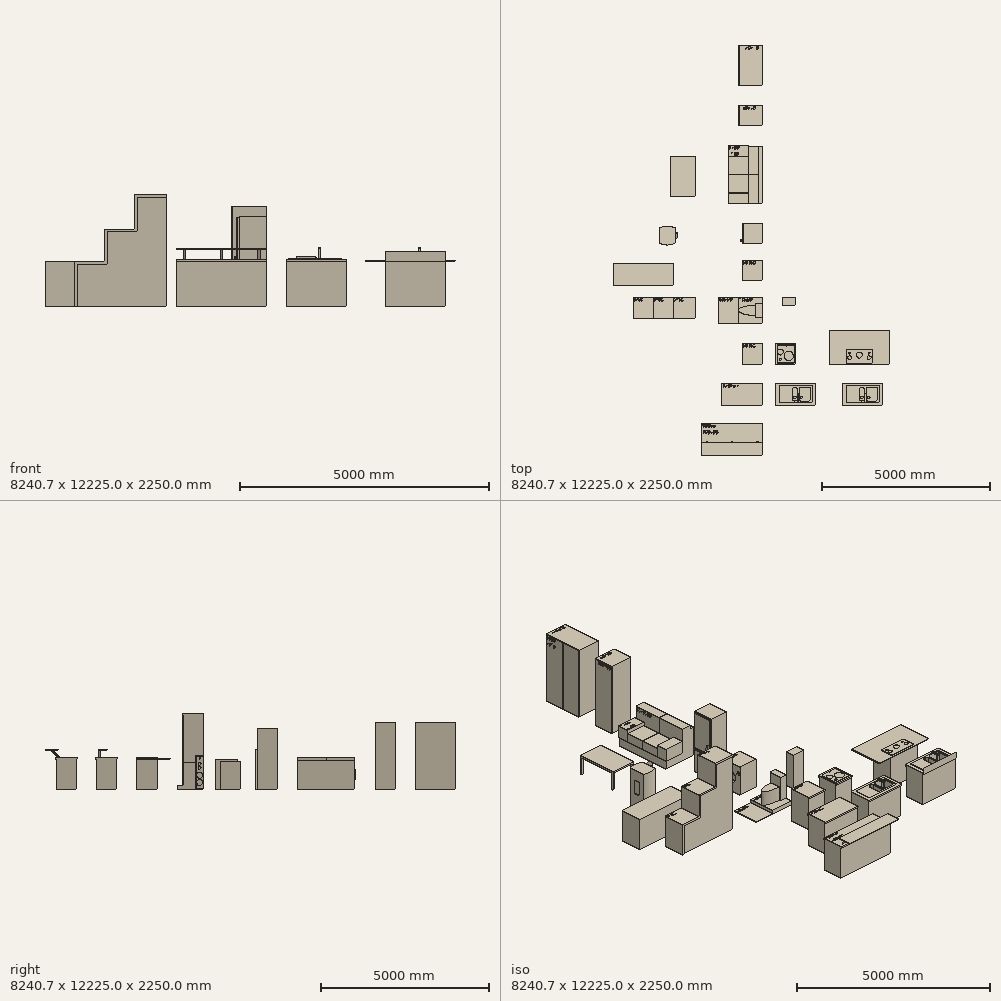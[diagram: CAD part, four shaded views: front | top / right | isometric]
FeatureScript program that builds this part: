
annotation { "Feature Type Name" : "Feature", "Feature Type Description" : "" }
export const myFeature = defineFeature(function(context is Context, id is Id, definition is map)
    precondition{}
    {
        {
            var Q0;
            Q0=qCreatedBy(makeId("Top.planeOp"),FACE);
            var sketch = newSketch(context, id + "F0", { "sketchPlane" : qUnion([Q0])});
            skLineSegment(sketch, "E0.bottom", {"start": v(0, 0) * mm, "end": v(-1300, 0) * mm});
            skLineSegment(sketch, "E0.top", {"start": v(0, -800) * mm, "end": v(-1300, -800) * mm});
            skLineSegment(sketch, "E0.left", {"start": v(0, 0) * mm, "end": v(0, -800) * mm});
            skLineSegment(sketch, "E0.right", {"start": v(-1300, 0) * mm, "end": v(-1300, -800) * mm});
            skSolve(sketch);
        }
        {
            var Q0;
            Q0 = qSketchRegion(id + "F0", true);
            extrude(context, id + "F1", {"entities" : qUnion([Q0]), "depth" : 11 * mm});
        }
        {
            var Q0;
            Q0=makeQuery(id+"F1.opExtrude","CAP_FACE",FACE,{"disambiguationData":[OSD([sQuery(id+"F0.wireOp",EDGE,"E0.bottom"),sQuery(id+"F0.wireOp",EDGE,"E0.top"),sQuery(id+"F0.wireOp",EDGE,"E0.left"),sQuery(id+"F0.wireOp",EDGE,"E0.right")])],"isStart":false});
            var sketch = newSketch(context, id + "F2", { "sketchPlane" : qUnion([Q0])});
            skLineSegment(sketch, "E1.bottom", {"start": v(0, 0) * mm, "end": v(-700, 0) * mm});
            skLineSegment(sketch, "E1.top", {"start": v(0, -800) * mm, "end": v(-700, -800) * mm});
            skLineSegment(sketch, "E1.left", {"start": v(0, 0) * mm, "end": v(0, -800) * mm});
            skLineSegment(sketch, "E1.right", {"start": v(-700, 0) * mm, "end": v(-700, -800) * mm});
            skSolve(sketch);
        }
        {
            var Q0;
            Q0 = qSketchRegion(id + "F2", true);
            extrude(context, id + "F3", {"entities" : qUnion([Q0]), "operationType" : NewBodyOperationType.ADD, "depth" : 100 * mm});
        }
        {
            var Q0;
            Q0=makeQuery(id+"F3.opExtrude","CAP_FACE",FACE,{"disambiguationData":[OSD([sQuery(id+"F2.wireOp",EDGE,"E1.bottom"),sQuery(id+"F2.wireOp",EDGE,"E1.top"),sQuery(id+"F2.wireOp",EDGE,"E1.left"),sQuery(id+"F2.wireOp",EDGE,"E1.right")])],"isStart":false});
            var sketch = newSketch(context, id + "F4", { "sketchPlane" : qUnion([Q0])});
            skLineSegment(sketch, "E2.bottom", {"start": v(0, -200) * mm, "end": v(-200, -200) * mm});
            skLineSegment(sketch, "E2.top", {"start": v(0, -600) * mm, "end": v(-200, -600) * mm});
            skLineSegment(sketch, "E2.left", {"start": v(0, -200) * mm, "end": v(0, -600) * mm});
            skLineSegment(sketch, "E2.right", {"start": v(-200, -200) * mm, "end": v(-200, -600) * mm});
            skSolve(sketch);
        }
        {
            var Q0;
            {var subQ2=sQuery(id+"F4.wireOp",EDGE,"E2.bottom");Q0=makeQuery(id+"F4.imprint","IMPRINT",FACE,{"disambiguationData":[TD([[makeQuery(id+"F4.imprint","IMPRINT",EDGE,{"derivedFrom":subQ2}),-1.0]])]});}
            var sketch = newSketch(context, id + "F5", { "sketchPlane" : qUnion([Q0])});
            skLineSegment(sketch, "E3", {"start": v(-200, -249.1) * mm, "end": v(-200, -549.1) * mm});
            skEllipticalArc(sketch, "E4", {});
            const initialGuessF5  = {"E4": [-0.2, -0.3990970113503016, 1, 0, 0.5000090601184898, 0.15, 1.5707963267948966, 4.71238898038469]};
            skSetInitialGuess(sketch, initialGuessF5);
            skSolve(sketch);
        }
        {
            var Q0;
            Q0 = qSketchRegion(id + "F4", true);
            extrude(context, id + "F6", {"entities" : qUnion([Q0]), "operationType" : NewBodyOperationType.ADD, "depth" : 700 * mm});
        }
        {
            var Q0;
            {var subQ0=sQuery(id+"F5.wireOp",EDGE,"E3");Q0=makeQuery(id+"F5.imprint","IMPRINT",FACE,{"disambiguationData":[TD([[makeQuery(id+"F5.imprint","IMPRINT",EDGE,{"derivedFrom":subQ0}),-1.0]])]});}
            extrude(context, id + "F7", {"entities" : qUnion([Q0]), "operationType" : NewBodyOperationType.ADD, "depth" : 400 * mm});
        }
        {
            var Q0;
            Q0=makeQuery(id+"F1.opExtrude","CAP_FACE",FACE,{"disambiguationData":[OSD([sQuery(id+"F0.wireOp",EDGE,"E0.bottom"),sQuery(id+"F0.wireOp",EDGE,"E0.top"),sQuery(id+"F0.wireOp",EDGE,"E0.left"),sQuery(id+"F0.wireOp",EDGE,"E0.right")])],"isStart":false});
            var sketch = newSketch(context, id + "F8", { "sketchPlane" : qUnion([Q0])});
            skText(sketch, "E5", { "text": "60x80", "fontName": "OpenSans-Regular.ttf"});
            const initialGuessF8  = {"E5": [-1.28, -0.12, 1, 0, 0.1]};
            skSetInitialGuess(sketch, initialGuessF8);
            skSolve(sketch);
        }
        {
            var Q0;
            Q0 = qSketchRegion(id + "F8", true);
            extrude(context, id + "F9", {"entities" : qUnion([Q0]), "operationType" : NewBodyOperationType.REMOVE, "oppositeDirection" : true, "depth" : 10 * mm});
        }
        {
            var Q0;
            {var subQ0=sQuery(id+"F2.wireOp",EDGE,"E1.left");var subQ1=sQuery(id+"F2.wireOp",EDGE,"E1.bottom");var subQ3=sQuery(id+"F2.wireOp",EDGE,"E1.right");Q0=makeQuery(id+"F7.boolean.opBoolean","SPLIT",FACE,{"disambiguationData":[TD([makeQuery(id+"F1.opExtrude","SWEPT_FACE",FACE,{"disambiguationData":[OSD([sQuery(id+"F0.wireOp",EDGE,"E0.bottom")])]})])],"derivedFrom":makeQuery(id+"F3.opExtrude","CAP_FACE",FACE,{"disambiguationData":[OSD([subQ1,sQuery(id+"F2.wireOp",EDGE,"E1.top"),subQ0,subQ3])],"isStart":false})});}
            var sketch = newSketch(context, id + "F10", { "sketchPlane" : qUnion([Q0])});
            skText(sketch, "E6", { "text": "70x80", "fontName": "OpenSans-Regular.ttf"});
            const initialGuessF10  = {"E6": [-0.68, -0.12, 1, 0, 0.1]};
            skSetInitialGuess(sketch, initialGuessF10);
            skSolve(sketch);
        }
        {
            var Q0;
            Q0 = qSketchRegion(id + "F10", true);
            extrude(context, id + "F11", {"entities" : qUnion([Q0]), "operationType" : NewBodyOperationType.REMOVE, "oppositeDirection" : true, "depth" : 10 * mm});
        }
        {
            var Q0;
            Q0=qCreatedBy(makeId("Top.planeOp"),FACE);
            var sketch = newSketch(context, id + "F12", { "sketchPlane" : qUnion([Q0])});
            skLineSegment(sketch, "E7.bottom", {"start": v(0, 500) * mm, "end": v(-600, 500) * mm});
            skLineSegment(sketch, "E7.top", {"start": v(0, 1100) * mm, "end": v(-600, 1100) * mm});
            skLineSegment(sketch, "E7.left", {"start": v(0, 500) * mm, "end": v(0, 1100) * mm});
            skLineSegment(sketch, "E7.right", {"start": v(-600, 500) * mm, "end": v(-600, 1100) * mm});
            skSolve(sketch);
        }
        {
            var Q0;
            Q0 = qSketchRegion(id + "F12", true);
            extrude(context, id + "F13", {"entities" : qUnion([Q0]), "depth" : 830 * mm});
        }
        {
            var Q0;
            Q0=makeQuery(id+"F13.opExtrude","SWEPT_FACE",FACE,{"disambiguationData":[OSD([sQuery(id+"F12.wireOp",EDGE,"E7.right")])]});
            var sketch = newSketch(context, id + "F14", { "sketchPlane" : qUnion([Q0])});
            skCircle(sketch, "E8", {"center": v(-800, 415) * mm, "radius": 150 * mm});
            skLineSegment(sketch, "E9", {"start": v(-1100, 415) * mm, "end": v(-500, 415) * mm, "construction": true});
            skLineSegment(sketch, "E10", {"start": v(-800, 0) * mm, "end": v(-800, 830) * mm, "construction": true});
            skSolve(sketch);
        }
        {
            var Q0;
            Q0=makeQuery(id+"F14.imprint","IMPRINT",FACE,{"disambiguationData":[TD([[makeQuery(id+"F14.imprint","IMPRINT",EDGE,{"derivedFrom":sQuery(id+"F14.wireOp",EDGE,"E8")}),1.0]])]});
            extrude(context, id + "F15", {"entities" : qUnion([Q0]), "operationType" : NewBodyOperationType.REMOVE, "oppositeDirection" : true, "depth" : 100 * mm});
        }
        {
            var Q0;
            Q0=makeQuery(id+"F13.opExtrude","CAP_FACE",FACE,{"disambiguationData":[OSD([sQuery(id+"F12.wireOp",EDGE,"E7.bottom"),sQuery(id+"F12.wireOp",EDGE,"E7.top"),sQuery(id+"F12.wireOp",EDGE,"E7.left"),sQuery(id+"F12.wireOp",EDGE,"E7.right")])],"isStart":false});
            var sketch = newSketch(context, id + "F16", { "sketchPlane" : qUnion([Q0])});
            skText(sketch, "E11", { "text": "60x60\n", "fontName": "OpenSans-Regular.ttf"});
            const initialGuessF16  = {"E11": [-0.58, 0.98, 1, 0, 0.1]};
            skSetInitialGuess(sketch, initialGuessF16);
            skSolve(sketch);
        }
        {
            var Q0;
            Q0 = qSketchRegion(id + "F16", true);
            extrude(context, id + "F17", {"entities" : qUnion([Q0]), "operationType" : NewBodyOperationType.REMOVE, "oppositeDirection" : true, "depth" : 10 * mm});
        }
        {
            var Q0;
            Q0=qCreatedBy(makeId("Front.planeOp"),FACE);
            var sketch = newSketch(context, id + "F18", { "sketchPlane" : qUnion([Q0])});
            skLineSegment(sketch, "E12", {"start": v(-2000, 2250) * mm, "end": v(-2000, 2200) * mm});
            skLineSegment(sketch, "E13", {"start": v(-2000, 2200) * mm, "end": v(-2600, 2200) * mm});
            skLineSegment(sketch, "E14", {"start": v(-2600, 2200) * mm, "end": v(-2600, 1500) * mm});
            skLineSegment(sketch, "E15", {"start": v(-2600, 1500) * mm, "end": v(-3200, 1500) * mm});
            skLineSegment(sketch, "E16", {"start": v(-3200, 1500) * mm, "end": v(-3200, 850) * mm});
            skLineSegment(sketch, "E17", {"start": v(-3200, 850) * mm, "end": v(-3800, 850) * mm});
            skLineSegment(sketch, "E18", {"start": v(-3800, 850) * mm, "end": v(-3800, 0) * mm});
            skLineSegment(sketch, "E19", {"start": v(-3800, 0) * mm, "end": v(-3850, 0) * mm});
            skLineSegment(sketch, "E20", {"start": v(-3850, 0) * mm, "end": v(-3850, 900) * mm});
            skLineSegment(sketch, "E21", {"start": v(-3850, 900) * mm, "end": v(-3250, 900) * mm});
            skLineSegment(sketch, "E22", {"start": v(-3250, 900) * mm, "end": v(-3250, 1550) * mm});
            skLineSegment(sketch, "E23", {"start": v(-3250, 1550) * mm, "end": v(-2650, 1550) * mm});
            skLineSegment(sketch, "E24", {"start": v(-2650, 1550) * mm, "end": v(-2650, 2250) * mm});
            skLineSegment(sketch, "E25", {"start": v(-2650, 2250) * mm, "end": v(-2000, 2250) * mm});
            skSolve(sketch);
        }
        {
            var Q0;
            Q0 = qSketchRegion(id + "F18", true);
            extrude(context, id + "F19", {"entities" : qUnion([Q0]), "depth" : 650 * mm});
        }
        {
            var Q0;
            Q0=makeQuery(id+"F19.opExtrude","SWEPT_FACE",FACE,{"disambiguationData":[OSD([sQuery(id+"F18.wireOp",EDGE,"E13")])]});
            var sketch = newSketch(context, id + "F20", { "sketchPlane" : qUnion([Q0])});
            skLineSegment(sketch, "E26.bottom", {"start": v(-2000, 625) * mm, "end": v(-2600, 625) * mm});
            skLineSegment(sketch, "E26.top", {"start": v(-2000, 25) * mm, "end": v(-2600, 25) * mm});
            skLineSegment(sketch, "E26.left", {"start": v(-2000, 625) * mm, "end": v(-2000, 25) * mm});
            skLineSegment(sketch, "E26.right", {"start": v(-2600, 625) * mm, "end": v(-2600, 25) * mm});
            skSolve(sketch);
        }
        {
            var Q0;
            Q0 = qSketchRegion(id + "F20", true);
            var Q1;
            Q1=qCreatedBy(makeId("Top.planeOp"),FACE);
            extrude(context, id + "F21", {"entities" : qUnion([Q0]), "operationType" : NewBodyOperationType.ADD, "endBound" : BoundingType.UP_TO_SURFACE, "endBoundEntityFace" : qUnion([Q1]), "depth" : 25 * mm});
        }
        {
            var Q0;
            Q0=makeQuery(id+"F19.opExtrude","SWEPT_FACE",FACE,{"disambiguationData":[OSD([sQuery(id+"F18.wireOp",EDGE,"E15")])]});
            var sketch = newSketch(context, id + "F22", { "sketchPlane" : qUnion([Q0])});
            skLineSegment(sketch, "E27.bottom", {"start": v(-2600, 25) * mm, "end": v(-3200, 25) * mm});
            skLineSegment(sketch, "E27.top", {"start": v(-2600, 625) * mm, "end": v(-3200, 625) * mm});
            skLineSegment(sketch, "E27.left", {"start": v(-2600, 25) * mm, "end": v(-2600, 625) * mm});
            skLineSegment(sketch, "E27.right", {"start": v(-3200, 25) * mm, "end": v(-3200, 625) * mm});
            skSolve(sketch);
        }
        {
            var Q0;
            Q0=makeQuery(id+"F22.imprint","IMPRINT",FACE,{"disambiguationData":[TD([[makeQuery(id+"F22.imprint","IMPRINT",EDGE,{"derivedFrom":sQuery(id+"F22.wireOp",EDGE,"E27.bottom")}),-1.0]])]});
            var Q1;
            Q1=qCreatedBy(makeId("Top.planeOp"),FACE);
            extrude(context, id + "F23", {"entities" : qUnion([Q0]), "operationType" : NewBodyOperationType.ADD, "endBound" : BoundingType.UP_TO_SURFACE, "endBoundEntityFace" : qUnion([Q1]), "depth" : 25 * mm});
        }
        {
            var Q0;
            Q0=makeQuery(id+"F19.opExtrude","SWEPT_FACE",FACE,{"disambiguationData":[OSD([sQuery(id+"F18.wireOp",EDGE,"E17")])]});
            var sketch = newSketch(context, id + "F24", { "sketchPlane" : qUnion([Q0])});
            skLineSegment(sketch, "E28.bottom", {"start": v(-3200, 25) * mm, "end": v(-3800, 25) * mm});
            skLineSegment(sketch, "E28.top", {"start": v(-3200, 625) * mm, "end": v(-3800, 625) * mm});
            skLineSegment(sketch, "E28.left", {"start": v(-3200, 25) * mm, "end": v(-3200, 625) * mm});
            skLineSegment(sketch, "E28.right", {"start": v(-3800, 25) * mm, "end": v(-3800, 625) * mm});
            skSolve(sketch);
        }
        {
            var Q0;
            Q0=makeQuery(id+"F24.imprint","IMPRINT",FACE,{"disambiguationData":[TD([[makeQuery(id+"F24.imprint","IMPRINT",EDGE,{"derivedFrom":sQuery(id+"F24.wireOp",EDGE,"E28.bottom")}),-1.0]])]});
            var Q1;
            Q1=qCreatedBy(makeId("Top.planeOp"),FACE);
            extrude(context, id + "F25", {"entities" : qUnion([Q0]), "operationType" : NewBodyOperationType.ADD, "endBound" : BoundingType.UP_TO_SURFACE, "endBoundEntityFace" : qUnion([Q1]), "depth" : 25 * mm});
        }
        {
            var Q0;
            Q0=makeQuery(id+"F19.opExtrude","CAP_FACE",FACE,{"disambiguationData":[OSD([sQuery(id+"F18.wireOp",EDGE,"E12"),sQuery(id+"F18.wireOp",EDGE,"E13"),sQuery(id+"F18.wireOp",EDGE,"E14"),sQuery(id+"F18.wireOp",EDGE,"E15"),sQuery(id+"F18.wireOp",EDGE,"E16"),sQuery(id+"F18.wireOp",EDGE,"E17"),sQuery(id+"F18.wireOp",EDGE,"E18"),sQuery(id+"F18.wireOp",EDGE,"E19"),sQuery(id+"F18.wireOp",EDGE,"E20"),sQuery(id+"F18.wireOp",EDGE,"E21"),sQuery(id+"F18.wireOp",EDGE,"E22"),sQuery(id+"F18.wireOp",EDGE,"E23"),sQuery(id+"F18.wireOp",EDGE,"E24"),sQuery(id+"F18.wireOp",EDGE,"E25")])],"isStart":true});
            var sketch = newSketch(context, id + "F26", { "sketchPlane" : qUnion([Q0])});
            skLineSegment(sketch, "E29.bottom", {"start": v(3850, 0) * mm, "end": v(2000, 0) * mm});
            skLineSegment(sketch, "E29.top", {"start": v(3850, 50) * mm, "end": v(3800, 50) * mm});
            skLineSegment(sketch, "E29.left", {"start": v(3850, 0) * mm, "end": v(3850, 50) * mm});
            skLineSegment(sketch, "E29.right", {"start": v(2000, 0) * mm, "end": v(2000, 50) * mm});
            skLineSegment(sketch, "E30.bottom", {"start": v(2600, 2200) * mm, "end": v(2599, 2200) * mm});
            skLineSegment(sketch, "E30.left", {"start": v(2600, 2200) * mm, "end": v(2600, 50) * mm});
            skLineSegment(sketch, "E30.right", {"start": v(2599, 2200) * mm, "end": v(2599, 50) * mm});
            skLineSegment(sketch, "E31.bottom", {"start": v(3200, 1500) * mm, "end": v(3199, 1500) * mm});
            skLineSegment(sketch, "E31.left", {"start": v(3200, 1500) * mm, "end": v(3200, 50) * mm});
            skLineSegment(sketch, "E31.right", {"start": v(3199, 1500) * mm, "end": v(3199, 50) * mm});
            skLineSegment(sketch, "E32.bottom", {"start": v(3800, 850) * mm, "end": v(3799, 850) * mm});
            skLineSegment(sketch, "E32.left", {"start": v(3800, 850) * mm, "end": v(3800, 50) * mm});
            skLineSegment(sketch, "E32.right", {"start": v(3799, 850) * mm, "end": v(3799, 50) * mm});
            skLineSegment(sketch, "E33.trimOffspring", {"start": v(2599, 50) * mm, "end": v(2000, 50) * mm});
            skLineSegment(sketch, "E34.trimOffspring", {"start": v(3199, 50) * mm, "end": v(2600, 50) * mm});
            skLineSegment(sketch, "E35.trimOffspring", {"start": v(3799, 50) * mm, "end": v(3200, 50) * mm});
            skSolve(sketch);
        }
        {
            var Q0;
            {var subQ10=sQuery(id+"F26.wireOp",EDGE,"E29.right");Q0=makeQuery(id+"F26.imprint","IMPRINT",FACE,{"disambiguationData":[TD([[makeQuery(id+"F26.imprint","IMPRINT",EDGE,{"derivedFrom":subQ10}),-1.0]])]});}
            extrude(context, id + "F27", {"entities" : qUnion([Q0]), "operationType" : NewBodyOperationType.REMOVE, "oppositeDirection" : true, "depth" : 35 * mm});
        }
        {
            var Q0;
            Q0=makeQuery(id+"F19.opExtrude","SWEPT_FACE",FACE,{"disambiguationData":[OSD([sQuery(id+"F18.wireOp",EDGE,"E25")])]});
            var sketch = newSketch(context, id + "F28", { "sketchPlane" : qUnion([Q0])});
            skText(sketch, "E36", { "text": "65x65", "fontName": "OpenSans-Regular.ttf"});
            const initialGuessF28  = {"E36": [-2.71922, -0.12, 1, 0, 0.1]};
            skSetInitialGuess(sketch, initialGuessF28);
            skSolve(sketch);
        }
        {
            var Q0;
            Q0 = qSketchRegion(id + "F28", true);
            extrude(context, id + "F29", {"entities" : qUnion([Q0]), "operationType" : NewBodyOperationType.REMOVE, "oppositeDirection" : true, "depth" : 10 * mm});
        }
        {
            var Q0;
            Q0=makeQuery(id+"F19.opExtrude","SWEPT_FACE",FACE,{"disambiguationData":[OSD([sQuery(id+"F18.wireOp",EDGE,"E23")])]});
            var sketch = newSketch(context, id + "F30", { "sketchPlane" : qUnion([Q0])});
            skText(sketch, "E37", { "text": "60x65", "fontName": "OpenSans-Regular.ttf"});
            const initialGuessF30  = {"E37": [-3.31922, -0.12, 1, 0, 0.1]};
            skSetInitialGuess(sketch, initialGuessF30);
            skSolve(sketch);
        }
        {
            var Q0;
            Q0 = qSketchRegion(id + "F30", true);
            extrude(context, id + "F31", {"entities" : qUnion([Q0]), "operationType" : NewBodyOperationType.REMOVE, "oppositeDirection" : true, "depth" : 10 * mm});
        }
        {
            var Q0;
            Q0=makeQuery(id+"F19.opExtrude","SWEPT_FACE",FACE,{"disambiguationData":[OSD([sQuery(id+"F18.wireOp",EDGE,"E21")])]});
            var sketch = newSketch(context, id + "F32", { "sketchPlane" : qUnion([Q0])});
            skText(sketch, "E38", { "text": "60x65", "fontName": "OpenSans-Regular.ttf"});
            const initialGuessF32  = {"E38": [-3.91922, -0.12, 1, 0, 0.1]};
            skSetInitialGuess(sketch, initialGuessF32);
            skSolve(sketch);
        }
        {
            var Q0;
            Q0 = qSketchRegion(id + "F32", true);
            extrude(context, id + "F33", {"entities" : qUnion([Q0]), "operationType" : NewBodyOperationType.REMOVE, "oppositeDirection" : true, "depth" : 10 * mm});
        }
        {
            var Q0;
            Q0=makeQuery(id+"F27.boolean.opBoolean","SPLIT",FACE,{"disambiguationData":[TD([makeQuery(id+"F19.opExtrude","SWEPT_FACE",FACE,{"disambiguationData":[OSD([sQuery(id+"F18.wireOp",EDGE,"E12")])]})])],"derivedFrom":makeQuery(id+"F25.boolean.opBoolean","MERGE",FACE,{"derivedFrom":[makeQuery(id+"F23.boolean.opBoolean","MERGE",FACE,{"derivedFrom":[makeQuery(id+"F21.opExtrude","SWEPT_FACE",FACE,{"disambiguationData":[OSD([sQuery(id+"F20.wireOp",EDGE,"E26.top")])]}),makeQuery(id+"F23.opExtrude","SWEPT_FACE",FACE,{"disambiguationData":[OSD([sQuery(id+"F22.wireOp",EDGE,"E27.bottom")])]})]}),makeQuery(id+"F25.opExtrude","SWEPT_FACE",FACE,{"disambiguationData":[OSD([sQuery(id+"F24.wireOp",EDGE,"E28.bottom")])]})]})});
            var sketch = newSketch(context, id + "F34", { "sketchPlane" : qUnion([Q0])});
            skText(sketch, "E39", { "text": "2200x60", "fontName": "OpenSans-Regular.ttf"});
            const initialGuessF34  = {"E39": [2.10922, 2.08, 1, 0, 0.1]};
            skSetInitialGuess(sketch, initialGuessF34);
            skSolve(sketch);
        }
        {
            var Q0;
            Q0 = qSketchRegion(id + "F34", true);
            extrude(context, id + "F35", {"entities" : qUnion([Q0]), "operationType" : NewBodyOperationType.REMOVE, "oppositeDirection" : true, "depth" : 10 * mm});
        }
        {
            var Q0;
            Q0=makeQuery(id+"F27.boolean.opBoolean","SPLIT",FACE,{"disambiguationData":[TD([makeQuery(id+"F19.opExtrude","SWEPT_FACE",FACE,{"disambiguationData":[OSD([sQuery(id+"F18.wireOp",EDGE,"E14")])]})])],"derivedFrom":makeQuery(id+"F25.boolean.opBoolean","MERGE",FACE,{"derivedFrom":[makeQuery(id+"F23.boolean.opBoolean","MERGE",FACE,{"derivedFrom":[makeQuery(id+"F21.opExtrude","SWEPT_FACE",FACE,{"disambiguationData":[OSD([sQuery(id+"F20.wireOp",EDGE,"E26.top")])]}),makeQuery(id+"F23.opExtrude","SWEPT_FACE",FACE,{"disambiguationData":[OSD([sQuery(id+"F22.wireOp",EDGE,"E27.bottom")])]})]}),makeQuery(id+"F25.opExtrude","SWEPT_FACE",FACE,{"disambiguationData":[OSD([sQuery(id+"F24.wireOp",EDGE,"E28.bottom")])]})]})});
            var sketch = newSketch(context, id + "F36", { "sketchPlane" : qUnion([Q0])});
            skText(sketch, "E40", { "text": "1500x60", "fontName": "OpenSans-Regular.ttf"});
            const initialGuessF36  = {"E40": [2.70922, 1.38, 1, 0, 0.1]};
            skSetInitialGuess(sketch, initialGuessF36);
            skSolve(sketch);
        }
        {
            var Q0;
            Q0 = qSketchRegion(id + "F36", true);
            extrude(context, id + "F37", {"entities" : qUnion([Q0]), "operationType" : NewBodyOperationType.REMOVE, "oppositeDirection" : true, "depth" : 10 * mm});
        }
        {
            var Q0;
            Q0=makeQuery(id+"F27.boolean.opBoolean","SPLIT",FACE,{"disambiguationData":[TD([makeQuery(id+"F19.opExtrude","SWEPT_FACE",FACE,{"disambiguationData":[OSD([sQuery(id+"F18.wireOp",EDGE,"E16")])]})])],"derivedFrom":makeQuery(id+"F25.boolean.opBoolean","MERGE",FACE,{"derivedFrom":[makeQuery(id+"F23.boolean.opBoolean","MERGE",FACE,{"derivedFrom":[makeQuery(id+"F21.opExtrude","SWEPT_FACE",FACE,{"disambiguationData":[OSD([sQuery(id+"F20.wireOp",EDGE,"E26.top")])]}),makeQuery(id+"F23.opExtrude","SWEPT_FACE",FACE,{"disambiguationData":[OSD([sQuery(id+"F22.wireOp",EDGE,"E27.bottom")])]})]}),makeQuery(id+"F25.opExtrude","SWEPT_FACE",FACE,{"disambiguationData":[OSD([sQuery(id+"F24.wireOp",EDGE,"E28.bottom")])]})]})});
            var sketch = newSketch(context, id + "F38", { "sketchPlane" : qUnion([Q0])});
            skText(sketch, "E41", { "text": "90x60", "fontName": "OpenSans-Regular.ttf"});
            const initialGuessF38  = {"E41": [3.30822, 0.73, 1, 0, 0.1]};
            skSetInitialGuess(sketch, initialGuessF38);
            skSolve(sketch);
        }
        {
            var Q0;
            Q0 = qSketchRegion(id + "F38", true);
            extrude(context, id + "F39", {"entities" : qUnion([Q0]), "operationType" : NewBodyOperationType.REMOVE, "oppositeDirection" : true, "depth" : 10 * mm});
        }
        {
            var Q0;
            Q0=qCreatedBy(makeId("Top.planeOp"),FACE);
            var sketch = newSketch(context, id + "F40", { "sketchPlane" : qUnion([Q0])});
            skLineSegment(sketch, "E42.bottom", {"start": v(0, 2200) * mm, "end": v(-550, 2200) * mm});
            skLineSegment(sketch, "E42.top", {"start": v(0, 1600) * mm, "end": v(-550, 1600) * mm});
            skLineSegment(sketch, "E42.left", {"start": v(0, 2200) * mm, "end": v(0, 1600) * mm});
            skLineSegment(sketch, "E42.right", {"start": v(-550, 2200) * mm, "end": v(-550, 1600) * mm});
            skSolve(sketch);
        }
        {
            var Q0;
            Q0 = qSketchRegion(id + "F40", true);
            extrude(context, id + "F41", {"entities" : qUnion([Q0]), "depth" : 1800 * mm});
        }
        {
            var Q0;
            Q0=makeQuery(id+"F41.opExtrude","SWEPT_FACE",FACE,{"disambiguationData":[OSD([sQuery(id+"F40.wireOp",EDGE,"E42.right")])]});
            var sketch = newSketch(context, id + "F42", { "sketchPlane" : qUnion([Q0])});
            skLineSegment(sketch, "E43.bottom", {"start": v(-2190, 10) * mm, "end": v(-1610, 10) * mm});
            skLineSegment(sketch, "E43.top", {"start": v(-2190, 710) * mm, "end": v(-1610, 710) * mm});
            skLineSegment(sketch, "E43.left", {"start": v(-2190, 10) * mm, "end": v(-2190, 710) * mm});
            skLineSegment(sketch, "E43.right", {"start": v(-1610, 10) * mm, "end": v(-1610, 710) * mm});
            skLineSegment(sketch, "E44.bottom", {"start": v(-2190, 720) * mm, "end": v(-1610, 720) * mm});
            skLineSegment(sketch, "E44.top", {"start": v(-2190, 1790) * mm, "end": v(-1610, 1790) * mm});
            skLineSegment(sketch, "E44.left", {"start": v(-2190, 720) * mm, "end": v(-2190, 1790) * mm});
            skLineSegment(sketch, "E44.right", {"start": v(-1610, 720) * mm, "end": v(-1610, 1790) * mm});
            skSolve(sketch);
        }
        {
            var Q0;
            Q0 = qSketchRegion(id + "F42", true);
            extrude(context, id + "F43", {"entities" : qUnion([Q0]), "operationType" : NewBodyOperationType.ADD, "depth" : 50 * mm});
        }
        {
            var Q0;
            Q0=makeQuery(id+"F43.opExtrude","CAP_FACE",FACE,{"disambiguationData":[OSD([sQuery(id+"F42.wireOp",EDGE,"E43.bottom"),sQuery(id+"F42.wireOp",EDGE,"E43.top"),sQuery(id+"F42.wireOp",EDGE,"E43.left"),sQuery(id+"F42.wireOp",EDGE,"E43.right")])],"isStart":false});
            var Q1;
            Q1=makeQuery(id+"F43.opExtrude","CAP_FACE",FACE,{"disambiguationData":[OSD([sQuery(id+"F42.wireOp",EDGE,"E44.bottom"),sQuery(id+"F42.wireOp",EDGE,"E44.top"),sQuery(id+"F42.wireOp",EDGE,"E44.left"),sQuery(id+"F42.wireOp",EDGE,"E44.right")])],"isStart":false});
            fillet(context, id + "F44", {"entities" : qUnion([Q0, Q1]), "radius" : 20 * mm, "tangentPropagation" : true, "allowEdgeOverflow" : false});
        }
        {
            var Q0;
            Q0=makeQuery(id+"F43.opExtrude","CAP_FACE",FACE,{"disambiguationData":[OSD([sQuery(id+"F42.wireOp",EDGE,"E44.bottom"),sQuery(id+"F42.wireOp",EDGE,"E44.top"),sQuery(id+"F42.wireOp",EDGE,"E44.left"),sQuery(id+"F42.wireOp",EDGE,"E44.right")])],"isStart":false});
            var sketch = newSketch(context, id + "F45", { "sketchPlane" : qUnion([Q0])});
            skCircle(sketch, "E45", {"center": v(-1680, 990) * mm, "radius": 10 * mm});
            skCircle(sketch, "E46", {"center": v(-1680, 790) * mm, "radius": 10 * mm});
            skCircle(sketch, "E47", {"center": v(-1680, 640) * mm, "radius": 10 * mm});
            skCircle(sketch, "E48", {"center": v(-1680, 440) * mm, "radius": 10 * mm});
            skLineSegment(sketch, "E49", {"start": v(-1680, 990) * mm, "end": v(-1680, 440) * mm, "construction": true});
            skSolve(sketch);
        }
        {
            var Q0;
            Q0 = qSketchRegion(id + "F45", true);
            extrude(context, id + "F46", {"entities" : qUnion([Q0]), "operationType" : NewBodyOperationType.ADD, "depth" : 30 * mm});
        }
        {
            var Q0;
            Q0=makeQuery(id+"F46.opExtrude","CAP_FACE",FACE,{"disambiguationData":[OSD([sQuery(id+"F45.wireOp",EDGE,"E45")])],"isStart":false});
            var sketch = newSketch(context, id + "F47", { "sketchPlane" : qUnion([Q0])});
            skLineSegment(sketch, "E50", {"start": v(-1680, 990) * mm, "end": v(-1680, 790) * mm, "construction": true});
            skEllipse(sketch, "E51", {"center": v(-1680, 890) * mm, "majorRadius": 110.23 * mm, "minorRadius": 30 * mm, "majorAxis": v(0, -1)});
            skLineSegment(sketch, "E52", {"start": v(-1680, 640) * mm, "end": v(-1680, 440) * mm, "construction": true});
            skEllipse(sketch, "E53", {"center": v(-1680, 540) * mm, "majorRadius": 110.23 * mm, "minorRadius": 30 * mm, "majorAxis": v(0, -1)});
            skSolve(sketch);
        }
        {
            var Q0;
            Q0 = qSketchRegion(id + "F47", true);
            extrude(context, id + "F48", {"entities" : qUnion([Q0]), "operationType" : NewBodyOperationType.ADD, "depth" : 10 * mm});
        }
        {
            var Q0;
            Q0=makeQuery(id+"F41.opExtrude","CAP_FACE",FACE,{"disambiguationData":[OSD([sQuery(id+"F40.wireOp",EDGE,"E42.bottom"),sQuery(id+"F40.wireOp",EDGE,"E42.top"),sQuery(id+"F40.wireOp",EDGE,"E42.left"),sQuery(id+"F40.wireOp",EDGE,"E42.right")])],"isStart":false});
            var sketch = newSketch(context, id + "F49", { "sketchPlane" : qUnion([Q0])});
            skText(sketch, "E54", { "text": "60x60", "fontName": "OpenSans-Regular.ttf"});
            const initialGuessF49  = {"E54": [-1.78006, 0.5736, 1, 0, 0.1]};
            skSetInitialGuess(sketch, initialGuessF49);
            skSolve(sketch);
        }
        {
            var Q0;
            Q0 = qSketchRegion(id + "F49", true);
            extrude(context, id + "F50", {"entities" : qUnion([Q0]), "operationType" : NewBodyOperationType.REMOVE, "oppositeDirection" : true, "depth" : 10 * mm});
        }
        {
            var Q0;
            Q0=makeQuery(id+"F43.opExtrude","CAP_FACE",FACE,{"disambiguationData":[OSD([sQuery(id+"F42.wireOp",EDGE,"E44.bottom"),sQuery(id+"F42.wireOp",EDGE,"E44.top"),sQuery(id+"F42.wireOp",EDGE,"E44.left"),sQuery(id+"F42.wireOp",EDGE,"E44.right")])],"isStart":false});
            var sketch = newSketch(context, id + "F51", { "sketchPlane" : qUnion([Q0])});
            skText(sketch, "E55", { "text": "1800", "fontName": "OpenSans-Regular.ttf"});
            const initialGuessF51  = {"E55": [-0.6436, 1.65, 1, 0, 0.1]};
            skSetInitialGuess(sketch, initialGuessF51);
            skSolve(sketch);
        }
        {
            var Q0;
            Q0 = qSketchRegion(id + "F51", true);
            extrude(context, id + "F52", {"entities" : qUnion([Q0]), "operationType" : NewBodyOperationType.REMOVE, "oppositeDirection" : true, "depth" : 10 * mm});
        }
        {
            var Q0;
            Q0=makeQuery(id+"F43.opExtrude","CAP_FACE",FACE,{"disambiguationData":[OSD([sQuery(id+"F42.wireOp",EDGE,"E43.bottom"),sQuery(id+"F42.wireOp",EDGE,"E43.top"),sQuery(id+"F42.wireOp",EDGE,"E43.left"),sQuery(id+"F42.wireOp",EDGE,"E43.right")])],"isStart":false});
            var sketch = newSketch(context, id + "F53", { "sketchPlane" : qUnion([Q0])});
            skText(sketch, "E56", { "text": "70", "fontName": "OpenSans-Regular.ttf"});
            const initialGuessF53  = {"E56": [-0.6436, 0.57, 1, 0, 0.1]};
            skSetInitialGuess(sketch, initialGuessF53);
            skSolve(sketch);
        }
        {
            var Q0;
            Q0 = qSketchRegion(id + "F53", true);
            extrude(context, id + "F54", {"entities" : qUnion([Q0]), "operationType" : NewBodyOperationType.REMOVE, "oppositeDirection" : true, "depth" : 10 * mm});
        }
        {
            var Q0;
            Q0=qCreatedBy(makeId("Top.planeOp"),FACE);
            var sketch = newSketch(context, id + "F55", { "sketchPlane" : qUnion([Q0])});
            skLineSegment(sketch, "E57.bottom", {"start": v(-2640.7, 335.34) * mm, "end": v(-4440.7, 335.34) * mm});
            skLineSegment(sketch, "E57.top", {"start": v(-2640.7, 985.34) * mm, "end": v(-4440.7, 985.34) * mm});
            skLineSegment(sketch, "E57.left", {"start": v(-2640.7, 335.34) * mm, "end": v(-2640.7, 985.34) * mm});
            skLineSegment(sketch, "E57.right", {"start": v(-4440.7, 335.34) * mm, "end": v(-4440.7, 985.34) * mm});
            skSolve(sketch);
        }
        {
            var Q0;
            Q0 = qSketchRegion(id + "F55", true);
            extrude(context, id + "F56", {"entities" : qUnion([Q0]), "depth" : 900 * mm});
        }
        {
            var Q0;
            Q0=qCreatedBy(makeId("Top.planeOp"),FACE);
            var sketch = newSketch(context, id + "F57", { "sketchPlane" : qUnion([Q0])});
            skLineSegment(sketch, "E58.bottom", {"start": v(-1000, 2800) * mm, "end": v(0, 2800) * mm});
            skLineSegment(sketch, "E58.top", {"start": v(-1000, 4500) * mm, "end": v(0, 4500) * mm});
            skLineSegment(sketch, "E58.left", {"start": v(-1000, 2800) * mm, "end": v(-1000, 4500) * mm});
            skLineSegment(sketch, "E58.right", {"start": v(0, 2800) * mm, "end": v(0, 4500) * mm});
            skSolve(sketch);
        }
        {
            var Q0;
            Q0 = qSketchRegion(id + "F57", true);
            extrude(context, id + "F58", {"entities" : qUnion([Q0]), "depth" : 250 * mm});
        }
        {
            var Q0;
            Q0=makeQuery(id+"F58.opExtrude","CAP_FACE",FACE,{"disambiguationData":[OSD([sQuery(id+"F57.wireOp",EDGE,"E58.bottom"),sQuery(id+"F57.wireOp",EDGE,"E58.top"),sQuery(id+"F57.wireOp",EDGE,"E58.left"),sQuery(id+"F57.wireOp",EDGE,"E58.right")])],"isStart":false});
            var sketch = newSketch(context, id + "F59", { "sketchPlane" : qUnion([Q0])});
            skLineSegment(sketch, "E59.bottom", {"start": v(0, 4500) * mm, "end": v(-100, 4500) * mm});
            skLineSegment(sketch, "E59.top", {"start": v(0, 2800) * mm, "end": v(-100, 2800) * mm});
            skLineSegment(sketch, "E59.left", {"start": v(0, 4500) * mm, "end": v(0, 2800) * mm});
            skLineSegment(sketch, "E59.right", {"start": v(-100, 4500) * mm, "end": v(-100, 2800) * mm});
            skSolve(sketch);
        }
        {
            var Q0;
            Q0 = qSketchRegion(id + "F59", true);
            extrude(context, id + "F60", {"entities" : qUnion([Q0]), "operationType" : NewBodyOperationType.ADD, "depth" : 600 * mm});
        }
        {
            var Q0;
            Q0=makeQuery(id+"F58.opExtrude","CAP_FACE",FACE,{"disambiguationData":[OSD([sQuery(id+"F57.wireOp",EDGE,"E58.bottom"),sQuery(id+"F57.wireOp",EDGE,"E58.top"),sQuery(id+"F57.wireOp",EDGE,"E58.left"),sQuery(id+"F57.wireOp",EDGE,"E58.right")])],"isStart":false});
            var sketch = newSketch(context, id + "F61", { "sketchPlane" : qUnion([Q0])});
            skLineSegment(sketch, "E60.bottom", {"start": v(-110, 4500) * mm, "end": v(-410, 4500) * mm});
            skLineSegment(sketch, "E60.top", {"start": v(-110, 3655) * mm, "end": v(-410, 3655) * mm});
            skLineSegment(sketch, "E60.left", {"start": v(-110, 4500) * mm, "end": v(-110, 3655) * mm});
            skLineSegment(sketch, "E60.right", {"start": v(-410, 4500) * mm, "end": v(-410, 3655) * mm});
            skLineSegment(sketch, "E61.bottom", {"start": v(-410, 2800) * mm, "end": v(-110, 2800) * mm});
            skLineSegment(sketch, "E61.top", {"start": v(-410, 3645) * mm, "end": v(-110, 3645) * mm});
            skLineSegment(sketch, "E61.left", {"start": v(-410, 2800) * mm, "end": v(-410, 3645) * mm});
            skLineSegment(sketch, "E61.right", {"start": v(-110, 2800) * mm, "end": v(-110, 3645) * mm});
            skSolve(sketch);
        }
        {
            var Q0;
            Q0 = qSketchRegion(id + "F61", true);
            extrude(context, id + "F62", {"entities" : qUnion([Q0]), "operationType" : NewBodyOperationType.ADD, "depth" : 700 * mm});
        }
        {
            var Q0;
            Q0=makeQuery(id+"F58.opExtrude","CAP_FACE",FACE,{"disambiguationData":[OSD([sQuery(id+"F57.wireOp",EDGE,"E58.bottom"),sQuery(id+"F57.wireOp",EDGE,"E58.top"),sQuery(id+"F57.wireOp",EDGE,"E58.left"),sQuery(id+"F57.wireOp",EDGE,"E58.right")])],"isStart":false});
            var sketch = newSketch(context, id + "F63", { "sketchPlane" : qUnion([Q0])});
            skLineSegment(sketch, "E62.bottom", {"start": v(-420, 4520) * mm, "end": v(-1020, 4520) * mm});
            skLineSegment(sketch, "E62.top", {"start": v(-420, 4200) * mm, "end": v(-1020, 4200) * mm});
            skLineSegment(sketch, "E62.left", {"start": v(-420, 4520) * mm, "end": v(-420, 4200) * mm});
            skLineSegment(sketch, "E62.right", {"start": v(-1020, 4520) * mm, "end": v(-1020, 4200) * mm});
            skLineSegment(sketch, "E63.bottom", {"start": v(-420, 2780) * mm, "end": v(-1020, 2780) * mm});
            skLineSegment(sketch, "E63.top", {"start": v(-420, 3100) * mm, "end": v(-1020, 3100) * mm});
            skLineSegment(sketch, "E63.left", {"start": v(-420, 2780) * mm, "end": v(-420, 3100) * mm});
            skLineSegment(sketch, "E63.right", {"start": v(-1020, 2780) * mm, "end": v(-1020, 3100) * mm});
            skSolve(sketch);
        }
        {
            var Q0;
            Q0 = qSketchRegion(id + "F63", true);
            extrude(context, id + "F64", {"entities" : qUnion([Q0]), "operationType" : NewBodyOperationType.ADD, "depth" : 350 * mm});
        }
        {
            var Q0;
            Q0=makeQuery(id+"F58.opExtrude","CAP_FACE",FACE,{"disambiguationData":[OSD([sQuery(id+"F57.wireOp",EDGE,"E58.bottom"),sQuery(id+"F57.wireOp",EDGE,"E58.top"),sQuery(id+"F57.wireOp",EDGE,"E58.left"),sQuery(id+"F57.wireOp",EDGE,"E58.right")])],"isStart":false});
            var sketch = newSketch(context, id + "F65", { "sketchPlane" : qUnion([Q0])});
            skLineSegment(sketch, "E64.bottom", {"start": v(-420, 4190) * mm, "end": v(-1020, 4190) * mm});
            skLineSegment(sketch, "E64.top", {"start": v(-420, 3655) * mm, "end": v(-1020, 3655) * mm});
            skLineSegment(sketch, "E64.left", {"start": v(-420, 4190) * mm, "end": v(-420, 3655) * mm});
            skLineSegment(sketch, "E64.right", {"start": v(-1020, 4190) * mm, "end": v(-1020, 3655) * mm});
            skLineSegment(sketch, "E65.bottom", {"start": v(-420, 3645) * mm, "end": v(-1020, 3645) * mm});
            skLineSegment(sketch, "E65.top", {"start": v(-420, 3110) * mm, "end": v(-1020, 3110) * mm});
            skLineSegment(sketch, "E65.left", {"start": v(-420, 3645) * mm, "end": v(-420, 3110) * mm});
            skLineSegment(sketch, "E65.right", {"start": v(-1020, 3645) * mm, "end": v(-1020, 3110) * mm});
            skSolve(sketch);
        }
        {
            var Q0;
            Q0 = qSketchRegion(id + "F65", true);
            extrude(context, id + "F66", {"entities" : qUnion([Q0]), "operationType" : NewBodyOperationType.ADD, "depth" : 250 * mm});
        }
        {
            var Q0;
            Q0=makeQuery(id+"F64.opExtrude","CAP_FACE",FACE,{"disambiguationData":[OSD([sQuery(id+"F63.wireOp",EDGE,"E62.bottom"),sQuery(id+"F63.wireOp",EDGE,"E62.top"),sQuery(id+"F63.wireOp",EDGE,"E62.left"),sQuery(id+"F63.wireOp",EDGE,"E62.right")])],"isStart":false});
            var sketch = newSketch(context, id + "F67", { "sketchPlane" : qUnion([Q0])});
            skText(sketch, "E66", { "text": "1700\nx100", "fontName": "OpenSans-Regular.ttf"});
            const initialGuessF67  = {"E66": [-1, 4.4, 1, 0, 0.1]};
            skSetInitialGuess(sketch, initialGuessF67);
            skSolve(sketch);
        }
        {
            var Q0;
            Q0 = qSketchRegion(id + "F67", true);
            extrude(context, id + "F68", {"entities" : qUnion([Q0]), "operationType" : NewBodyOperationType.REMOVE, "oppositeDirection" : true, "depth" : 10 * mm});
        }
        {
            var Q0;
            Q0=makeQuery(id+"F62.opExtrude","SWEPT_FACE",FACE,{"disambiguationData":[OSD([sQuery(id+"F61.wireOp",EDGE,"E60.right")])]});
            var sketch = newSketch(context, id + "F69", { "sketchPlane" : qUnion([Q0])});
            skText(sketch, "E67", { "text": "95x1700", "fontName": "OpenSans-Regular.ttf"});
            const initialGuessF69  = {"E67": [-4.48, 0.83, 1, 0, 0.1]};
            skSetInitialGuess(sketch, initialGuessF69);
            skSolve(sketch);
        }
        {
            var Q0;
            Q0 = qSketchRegion(id + "F69", true);
            extrude(context, id + "F70", {"entities" : qUnion([Q0]), "operationType" : NewBodyOperationType.REMOVE, "oppositeDirection" : true, "depth" : 10 * mm});
        }
        {
            var Q0;
            Q0=qCreatedBy(makeId("Top.planeOp"),FACE);
            var sketch = newSketch(context, id + "F71", { "sketchPlane" : qUnion([Q0])});
            skLineSegment(sketch, "E68.bottom", {"start": v(0, 5100) * mm, "end": v(-700, 5100) * mm});
            skLineSegment(sketch, "E68.left", {"start": v(0, 5100) * mm, "end": v(0, 5700) * mm});
            skLineSegment(sketch, "E69", {"start": v(-700, 5100) * mm, "end": v(-700, 5700) * mm});
            skLineSegment(sketch, "E70", {"start": v(-700, 5700) * mm, "end": v(0, 5700) * mm});
            skSolve(sketch);
        }
        {
            var Q0;
            Q0 = qSketchRegion(id + "F71", true);
            extrude(context, id + "F72", {"entities" : qUnion([Q0]), "depth" : 2000 * mm});
        }
        {
            var Q0;
            Q0=makeQuery(id+"F72.opExtrude","CAP_FACE",FACE,{"disambiguationData":[OSD([sQuery(id+"F71.wireOp",EDGE,"E68.bottom"),sQuery(id+"F71.wireOp",EDGE,"E68.left"),sQuery(id+"F71.wireOp",EDGE,"E69"),sQuery(id+"F71.wireOp",EDGE,"E70")])],"isStart":false});
            var sketch = newSketch(context, id + "F73", { "sketchPlane" : qUnion([Q0])});
            skText(sketch, "E71", { "text": "60x70", "fontName": "OpenSans-Regular.ttf"});
            const initialGuessF73  = {"E71": [-0.58, 5.58, 1, 0, 0.1]};
            skSetInitialGuess(sketch, initialGuessF73);
            skSolve(sketch);
        }
        {
            var Q0;
            Q0 = qSketchRegion(id + "F73", true);
            extrude(context, id + "F74", {"entities" : qUnion([Q0]), "operationType" : NewBodyOperationType.REMOVE, "oppositeDirection" : true, "depth" : 10 * mm});
        }
        {
            var Q0;
            Q0=qCreatedBy(makeId("Top.planeOp"),FACE);
            var sketch = newSketch(context, id + "F75", { "sketchPlane" : qUnion([Q0])});
            skLineSegment(sketch, "E72.bottom", {"start": v(0, 6300) * mm, "end": v(-700, 6300) * mm});
            skLineSegment(sketch, "E72.top", {"start": v(0, 7500) * mm, "end": v(-700, 7500) * mm});
            skLineSegment(sketch, "E72.left", {"start": v(0, 6300) * mm, "end": v(0, 7500) * mm});
            skLineSegment(sketch, "E72.right", {"start": v(-700, 6300) * mm, "end": v(-700, 7500) * mm});
            skSolve(sketch);
        }
        {
            var Q0;
            Q0 = qSketchRegion(id + "F75", true);
            extrude(context, id + "F76", {"entities" : qUnion([Q0]), "depth" : 2000 * mm});
        }
        {
            var Q0;
            Q0=makeQuery(id+"F76.opExtrude","CAP_FACE",FACE,{"disambiguationData":[OSD([sQuery(id+"F75.wireOp",EDGE,"E72.bottom"),sQuery(id+"F75.wireOp",EDGE,"E72.top"),sQuery(id+"F75.wireOp",EDGE,"E72.left"),sQuery(id+"F75.wireOp",EDGE,"E72.right")])],"isStart":false});
            var sketch = newSketch(context, id + "F77", { "sketchPlane" : qUnion([Q0])});
            skText(sketch, "E73", { "text": "120x70", "fontName": "OpenSans-Regular.ttf"});
            const initialGuessF77  = {"E73": [-0.58, 7.38, 1, 0, 0.1]};
            skSetInitialGuess(sketch, initialGuessF77);
            skSolve(sketch);
        }
        {
            var Q0;
            Q0 = qSketchRegion(id + "F77", true);
            extrude(context, id + "F78", {"entities" : qUnion([Q0]), "operationType" : NewBodyOperationType.REMOVE, "oppositeDirection" : true, "depth" : 10 * mm});
        }
        {
            var Q0;
            Q0=makeQuery(id+"F72.opExtrude","SWEPT_FACE",FACE,{"disambiguationData":[OSD([sQuery(id+"F71.wireOp",EDGE,"E69")])]});
            var sketch = newSketch(context, id + "F79", { "sketchPlane" : qUnion([Q0])});
            skText(sketch, "E74", { "text": "2000x60", "fontName": "OpenSans-Regular.ttf"});
            const initialGuessF79  = {"E74": [-5.68, 1.88, 1, 0, 0.1]};
            skSetInitialGuess(sketch, initialGuessF79);
            skSolve(sketch);
        }
        {
            var Q0;
            Q0=makeQuery(id+"F76.opExtrude","SWEPT_FACE",FACE,{"disambiguationData":[OSD([sQuery(id+"F75.wireOp",EDGE,"E72.right")])]});
            var sketch = newSketch(context, id + "F80", { "sketchPlane" : qUnion([Q0])});
            skText(sketch, "E75", { "text": "2000\nx120", "fontName": "OpenSans-Regular.ttf"});
            const initialGuessF80  = {"E75": [-7.48, 1.88, 1, 0, 0.1]};
            skSetInitialGuess(sketch, initialGuessF80);
            skSolve(sketch);
        }
        {
            var Q0;
            {var subQ1=sQuery(id+"F75.wireOp",EDGE,"E72.right");var subQ3=sQuery(id+"F75.wireOp",EDGE,"E72.bottom");Q0=makeQuery(id+"F85.boolean.opBoolean","SPLIT",FACE,{"disambiguationData":[TD([makeQuery(id+"F76.opExtrude","SWEPT_FACE",FACE,{"disambiguationData":[OSD([subQ3])]})])],"derivedFrom":makeQuery(id+"F76.opExtrude","SWEPT_FACE",FACE,{"disambiguationData":[OSD([subQ1])]})});}
            var sketch = newSketch(context, id + "F81", { "sketchPlane" : qUnion([Q0])});
            skLineSegment(sketch, "E76.bottom", {"start": v(-6890, 0) * mm, "end": v(-6910, 0) * mm});
            skLineSegment(sketch, "E76.top", {"start": v(-6890, 2000) * mm, "end": v(-6910, 2000) * mm});
            skLineSegment(sketch, "E76.left", {"start": v(-6890, 0) * mm, "end": v(-6890, 2000) * mm});
            skLineSegment(sketch, "E76.right", {"start": v(-6910, 0) * mm, "end": v(-6910, 2000) * mm});
            skSolve(sketch);
        }
        {
            var Q0;
            Q0 = qSketchRegion(id + "F81", true);
            extrude(context, id + "F82", {"entities" : qUnion([Q0]), "operationType" : NewBodyOperationType.REMOVE, "oppositeDirection" : true, "depth" : 10 * mm});
        }
        {
            var Q0;
            {var subQ0=sQuery(id+"F75.wireOp",EDGE,"E72.bottom");var subQ1=makeQuery(id+"F76.opExtrude","SWEPT_FACE",FACE,{"disambiguationData":[OSD([subQ0])]});var subQ2=sQuery(id+"F75.wireOp",EDGE,"E72.right");Q0=makeQuery(id+"F82.boolean.opBoolean","SPLIT",FACE,{"disambiguationData":[TD([subQ1])],"derivedFrom":makeQuery(id+"F85.boolean.opBoolean","SPLIT",FACE,{"disambiguationData":[TD([subQ1])],"derivedFrom":makeQuery(id+"F76.opExtrude","SWEPT_FACE",FACE,{"disambiguationData":[OSD([subQ2])]})})});}
            var Q1;
            {var subQ11=sQuery(id+"F75.wireOp",EDGE,"E72.top");var subQ12=makeQuery(id+"F76.opExtrude","SWEPT_FACE",FACE,{"disambiguationData":[OSD([subQ11])]});var subQ14=sQuery(id+"F75.wireOp",EDGE,"E72.right");var subQ16=sQuery(id+"F75.wireOp",EDGE,"E72.bottom");Q1=makeQuery(id+"F82.boolean.opBoolean","SPLIT",FACE,{"disambiguationData":[TD([subQ12])],"derivedFrom":makeQuery(id+"F85.boolean.opBoolean","SPLIT",FACE,{"disambiguationData":[TD([makeQuery(id+"F76.opExtrude","SWEPT_FACE",FACE,{"disambiguationData":[OSD([subQ16])]})])],"derivedFrom":makeQuery(id+"F76.opExtrude","SWEPT_FACE",FACE,{"disambiguationData":[OSD([subQ14])]})})});}
            var Q2;
            {var subQ1=sQuery(id+"F71.wireOp",EDGE,"E69");var subQ3=sQuery(id+"F71.wireOp",EDGE,"E68.bottom");Q2=makeQuery(id+"F84.boolean.opBoolean","SPLIT",FACE,{"disambiguationData":[TD([makeQuery(id+"F72.opExtrude","SWEPT_FACE",FACE,{"disambiguationData":[OSD([subQ3])]})])],"derivedFrom":makeQuery(id+"F72.opExtrude","SWEPT_FACE",FACE,{"disambiguationData":[OSD([subQ1])]})});}
            fillet(context, id + "F83", {"entities" : qUnion([Q0, Q1, Q2]), "radius" : 10 * mm, "tangentPropagation" : true, "allowEdgeOverflow" : false});
        }
        {
            var Q0;
            Q0 = qSketchRegion(id + "F79", true);
            extrude(context, id + "F84", {"entities" : qUnion([Q0]), "operationType" : NewBodyOperationType.REMOVE, "oppositeDirection" : true, "depth" : 10 * mm});
        }
        {
            var Q0;
            Q0 = qSketchRegion(id + "F80", true);
            extrude(context, id + "F85", {"entities" : qUnion([Q0]), "operationType" : NewBodyOperationType.REMOVE, "oppositeDirection" : true, "depth" : 10 * mm});
        }
        {
            var Q0;
            Q0=qCreatedBy(makeId("Top.planeOp"),FACE);
            var sketch = newSketch(context, id + "F86", { "sketchPlane" : qUnion([Q0])});
            skLineSegment(sketch, "E77.bottom", {"start": v(600, 0) * mm, "end": v(1000, 0) * mm});
            skLineSegment(sketch, "E77.top", {"start": v(600, -250) * mm, "end": v(1000, -250) * mm});
            skLineSegment(sketch, "E77.left", {"start": v(600, 0) * mm, "end": v(600, -250) * mm});
            skLineSegment(sketch, "E77.right", {"start": v(1000, 0) * mm, "end": v(1000, -250) * mm});
            skSolve(sketch);
        }
        {
            var Q0;
            Q0 = qSketchRegion(id + "F86", true);
            extrude(context, id + "F87", {"entities" : qUnion([Q0]), "depth" : 1000 * mm});
        }
        {
            var Q0;
            Q0=makeQuery(id+"F87.opExtrude","SWEPT_FACE",FACE,{"disambiguationData":[OSD([sQuery(id+"F86.wireOp",EDGE,"E77.right")])]});
            chamfer(context, id + "F88", {"entities" : qUnion([Q0]), "width" : 15 * mm, "tangentPropagation" : true});
        }
        {
            var Q0;
            Q0=makeQuery(id+"F87.opExtrude","SWEPT_FACE",FACE,{"disambiguationData":[OSD([sQuery(id+"F86.wireOp",EDGE,"E77.right")])]});
            var sketch = newSketch(context, id + "F89", { "sketchPlane" : qUnion([Q0])});
            skCircle(sketch, "E78", {"center": v(-125, 755) * mm, "radius": 45 * mm});
            skCircle(sketch, "E79", {"center": v(-125, 635) * mm, "radius": 45 * mm});
            skCircle(sketch, "E80", {"center": v(-125, 415) * mm, "radius": 90 * mm});
            skCircle(sketch, "E81", {"center": v(-125, 195) * mm, "radius": 90 * mm});
            skCircle(sketch, "E82", {"center": v(-125, 915) * mm, "radius": 20 * mm});
            skLineSegment(sketch, "E83", {"start": v(-125, 985) * mm, "end": v(-125, 15) * mm, "construction": true});
            skLineSegment(sketch, "E84", {"start": v(-15, 985) * mm, "end": v(-125, 985) * mm, "construction": true});
            skLineSegment(sketch, "E85", {"start": v(-125, 985) * mm, "end": v(-235, 985) * mm, "construction": true});
            skSolve(sketch);
        }
        {
            var Q0;
            Q0 = qSketchRegion(id + "F89", true);
            extrude(context, id + "F90", {"entities" : qUnion([Q0]), "operationType" : NewBodyOperationType.REMOVE, "oppositeDirection" : true, "depth" : 15 * mm});
        }
        {
            var Q0;
            Q0=qCreatedBy(makeId("Right.planeOp"),FACE);
            var sketch = newSketch(context, id + "F91", { "sketchPlane" : qUnion([Q0])});
            skLineSegment(sketch, "E86", {"start": v(-1400, 0) * mm, "end": v(-1400, 900) * mm});
            skLineSegment(sketch, "E87", {"start": v(-1400, 900) * mm, "end": v(-1375, 900) * mm});
            skLineSegment(sketch, "E88", {"start": v(-1375, 900) * mm, "end": v(-1375, 950) * mm});
            skLineSegment(sketch, "E89", {"start": v(-1375, 950) * mm, "end": v(-2025, 950) * mm});
            skLineSegment(sketch, "E90", {"start": v(-2025, 950) * mm, "end": v(-2025, 900) * mm});
            skLineSegment(sketch, "E91", {"start": v(-2025, 900) * mm, "end": v(-2000, 900) * mm});
            skLineSegment(sketch, "E92", {"start": v(-2000, 900) * mm, "end": v(-2000, 0) * mm});
            skLineSegment(sketch, "E93", {"start": v(-2000, 0) * mm, "end": v(-1400, 0) * mm});
            skSolve(sketch);
        }
        {
            var Q0;
            Q0 = qSketchRegion(id + "F91", true);
            extrude(context, id + "F92", {"entities" : qUnion([Q0]), "oppositeDirection" : true, "depth" : 600 * mm});
        }
        {
            var Q0;
            Q0=qCreatedBy(makeId("Right.planeOp"),FACE);
            var sketch = newSketch(context, id + "F93", { "sketchPlane" : qUnion([Q0])});
            skLineSegment(sketch, "E94", {"start": v(-2600, 0) * mm, "end": v(-2600, 900) * mm});
            skLineSegment(sketch, "E95", {"start": v(-2600, 900) * mm, "end": v(-2575, 900) * mm});
            skLineSegment(sketch, "E96", {"start": v(-2575, 900) * mm, "end": v(-2575, 950) * mm});
            skLineSegment(sketch, "E97", {"start": v(-2575, 950) * mm, "end": v(-3225, 950) * mm});
            skLineSegment(sketch, "E98", {"start": v(-3225, 950) * mm, "end": v(-3225, 900) * mm});
            skLineSegment(sketch, "E99", {"start": v(-3225, 900) * mm, "end": v(-3200, 900) * mm});
            skLineSegment(sketch, "E100", {"start": v(-3200, 900) * mm, "end": v(-3200, 0) * mm});
            skLineSegment(sketch, "E101", {"start": v(-3200, 0) * mm, "end": v(-2600, 0) * mm});
            skSolve(sketch);
        }
        {
            var Q0;
            Q0 = qSketchRegion(id + "F93", true);
            extrude(context, id + "F94", {"entities" : qUnion([Q0]), "oppositeDirection" : true, "depth" : 1200 * mm});
        }
        {
            var Q0;
            Q0=makeQuery(id+"F92.opExtrude","SWEPT_BODY",BODY,{"disambiguationData":[OSD([sQuery(id+"F91.wireOp",EDGE,"E86"),sQuery(id+"F91.wireOp",EDGE,"E87"),sQuery(id+"F91.wireOp",EDGE,"E88"),sQuery(id+"F91.wireOp",EDGE,"E89"),sQuery(id+"F91.wireOp",EDGE,"E90"),sQuery(id+"F91.wireOp",EDGE,"E91"),sQuery(id+"F91.wireOp",EDGE,"E92"),sQuery(id+"F91.wireOp",EDGE,"E93")])]});
            transform(context, id + "F95", {"entities" : qUnion([Q0]), "transformType" : TransformType.TRANSLATION_3D, "dx" : 1000 * mm, "dy" : 0 * mm, "dz" : 0 * mm, "makeCopy" : true});
        }
        {
            var Q0;
            Q0=makeQuery(id+"F95.opPattern","COPY",FACE,{"derivedFrom":makeQuery(id+"F92.opExtrude","SWEPT_FACE",FACE,{"disambiguationData":[OSD([sQuery(id+"F91.wireOp",EDGE,"E89")])]}),"instanceName":"1"});
            var sketch = newSketch(context, id + "F96", { "sketchPlane" : qUnion([Q0])});
            skLineSegment(sketch, "E102.bottom", {"start": v(450, -1975) * mm, "end": v(950, -1975) * mm});
            skLineSegment(sketch, "E102.top", {"start": v(450, -1425) * mm, "end": v(950, -1425) * mm});
            skLineSegment(sketch, "E102.left", {"start": v(450, -1975) * mm, "end": v(450, -1425) * mm});
            skLineSegment(sketch, "E102.right", {"start": v(950, -1975) * mm, "end": v(950, -1425) * mm});
            skSolve(sketch);
        }
        {
            var Q0;
            Q0 = qSketchRegion(id + "F96", true);
            extrude(context, id + "F97", {"entities" : qUnion([Q0]), "operationType" : NewBodyOperationType.ADD, "depth" : 5 * mm});
        }
        {
            var Q0;
            Q0=makeQuery(id+"F97.opExtrude","CAP_EDGE",EDGE,{"disambiguationData":[OSD([sQuery(id+"F96.wireOp",EDGE,"E102.bottom")])],"isStart":false});
            var Q1;
            Q1=makeQuery(id+"F97.opExtrude","CAP_EDGE",EDGE,{"disambiguationData":[OSD([sQuery(id+"F96.wireOp",EDGE,"E102.top")])],"isStart":false});
            chamfer(context, id + "F98", {"entities" : qUnion([Q0, Q1]), "chamferType" : ChamferType.OFFSET_ANGLE, "width" : 15 * mm, "oppositeDirection" : false, "angle" : 25 * degree, "tangentPropagation" : true});
        }
        {
            var Q0;
            Q0=makeQuery(id+"F97.opExtrude","CAP_FACE",FACE,{"disambiguationData":[OSD([sQuery(id+"F96.wireOp",EDGE,"E102.bottom"),sQuery(id+"F96.wireOp",EDGE,"E102.top"),sQuery(id+"F96.wireOp",EDGE,"E102.left"),sQuery(id+"F96.wireOp",EDGE,"E102.right")])],"isStart":false});
            var sketch = newSketch(context, id + "F99", { "sketchPlane" : qUnion([Q0])});
            skCircle(sketch, "E103", {"center": v(550, -1860) * mm, "radius": 40 * mm});
            skCircle(sketch, "E104", {"center": v(550, -1640) * mm, "radius": 90 * mm});
            skCircle(sketch, "E105", {"center": v(790, -1760) * mm, "radius": 140 * mm});
            skCircle(sketch, "E106", {"center": v(736.27, -1468.22) * mm, "radius": 14 * mm});
            skCircle(sketch, "E107", {"center": v(683.17, -1468.22) * mm, "radius": 9 * mm});
            skCircle(sketch, "E108", {"center": v(629.51, -1468.22) * mm, "radius": 4 * mm});
            skLineSegment(sketch, "E109.bottom", {"start": v(550, -1860) * mm, "end": v(790, -1860) * mm, "construction": true});
            skLineSegment(sketch, "E109.top", {"start": v(550, -1516.13) * mm, "end": v(790, -1516.13) * mm, "construction": true});
            skLineSegment(sketch, "E109.left", {"start": v(550, -1860) * mm, "end": v(550, -1516.13) * mm, "construction": true});
            skLineSegment(sketch, "E109.right", {"start": v(790, -1860) * mm, "end": v(790, -1516.13) * mm, "construction": true});
            skLineSegment(sketch, "E110", {"start": v(573.4, -1468.22) * mm, "end": v(816.2, -1468.22) * mm, "construction": true});
            skSolve(sketch);
        }
        {
            var Q0;
            Q0 = qSketchRegion(id + "F99", true);
            extrude(context, id + "F100", {"entities" : qUnion([Q0]), "operationType" : NewBodyOperationType.REMOVE, "oppositeDirection" : true, "depth" : 10 * mm});
        }
        {
            var Q0;
            Q0=makeQuery(id+"F94.opExtrude","SWEPT_BODY",BODY,{"disambiguationData":[OSD([sQuery(id+"F93.wireOp",EDGE,"E94"),sQuery(id+"F93.wireOp",EDGE,"E95"),sQuery(id+"F93.wireOp",EDGE,"E96"),sQuery(id+"F93.wireOp",EDGE,"E97"),sQuery(id+"F93.wireOp",EDGE,"E98"),sQuery(id+"F93.wireOp",EDGE,"E99"),sQuery(id+"F93.wireOp",EDGE,"E100"),sQuery(id+"F93.wireOp",EDGE,"E101")])]});
            transform(context, id + "F101", {"entities" : qUnion([Q0]), "transformType" : TransformType.TRANSLATION_3D, "dx" : 1600 * mm, "dy" : 0 * mm, "dz" : 0 * mm, "makeCopy" : true});
        }
        {
            var Q0;
            Q0=makeQuery(id+"F101.opPattern","COPY",FACE,{"derivedFrom":makeQuery(id+"F94.opExtrude","SWEPT_FACE",FACE,{"disambiguationData":[OSD([sQuery(id+"F93.wireOp",EDGE,"E97")])]}),"instanceName":"1"});
            var sketch = newSketch(context, id + "F102", { "sketchPlane" : qUnion([Q0])});
            skLineSegment(sketch, "E111.bottom", {"start": v(500, -3150) * mm, "end": v(1500, -3150) * mm});
            skLineSegment(sketch, "E111.top", {"start": v(500, -2650) * mm, "end": v(1500, -2650) * mm});
            skLineSegment(sketch, "E111.left", {"start": v(500, -3150) * mm, "end": v(500, -2650) * mm});
            skLineSegment(sketch, "E111.right", {"start": v(1500, -3150) * mm, "end": v(1500, -2650) * mm});
            skSolve(sketch);
        }
        {
            var Q0;
            Q0 = qSketchRegion(id + "F102", true);
            extrude(context, id + "F103", {"entities" : qUnion([Q0]), "operationType" : NewBodyOperationType.ADD, "depth" : 10 * mm});
        }
        {
            var Q0;
            Q0=makeQuery(id+"F103.opExtrude","SWEPT_EDGE",EDGE,{"disambiguationData":[OSD([sQuery(id+"F102.wireOp",EDGE,"E111.bottom"),sQuery(id+"F102.wireOp",EDGE,"E111.left")])]});
            var Q1;
            Q1=makeQuery(id+"F103.opExtrude","SWEPT_EDGE",EDGE,{"disambiguationData":[OSD([sQuery(id+"F102.wireOp",EDGE,"E111.top"),sQuery(id+"F102.wireOp",EDGE,"E111.left")])]});
            var Q2;
            Q2=makeQuery(id+"F103.opExtrude","SWEPT_EDGE",EDGE,{"disambiguationData":[OSD([sQuery(id+"F102.wireOp",EDGE,"E111.top"),sQuery(id+"F102.wireOp",EDGE,"E111.right")])]});
            var Q3;
            Q3=makeQuery(id+"F103.opExtrude","SWEPT_EDGE",EDGE,{"disambiguationData":[OSD([sQuery(id+"F102.wireOp",EDGE,"E111.bottom"),sQuery(id+"F102.wireOp",EDGE,"E111.right")])]});
            fillet(context, id + "F104", {"entities" : qUnion([Q0, Q1, Q2, Q3]), "radius" : 20 * mm, "tangentPropagation" : true, "allowEdgeOverflow" : false});
        }
        {
            var Q0;
            Q0=makeQuery(id+"F103.opExtrude","CAP_FACE",FACE,{"disambiguationData":[OSD([sQuery(id+"F102.wireOp",EDGE,"E111.bottom"),sQuery(id+"F102.wireOp",EDGE,"E111.top"),sQuery(id+"F102.wireOp",EDGE,"E111.left"),sQuery(id+"F102.wireOp",EDGE,"E111.right")])],"isStart":false});
            var sketch = newSketch(context, id + "F105", { "sketchPlane" : qUnion([Q0])});
            skLineSegment(sketch, "E112.bottom", {"start": v(1450, -2700) * mm, "end": v(1100, -2700) * mm});
            skLineSegment(sketch, "E112.top", {"start": v(1450, -3100) * mm, "end": v(1100, -3100) * mm});
            skLineSegment(sketch, "E112.left", {"start": v(1450, -2700) * mm, "end": v(1450, -3100) * mm});
            skLineSegment(sketch, "E112.right", {"start": v(1100, -2700) * mm, "end": v(1100, -3100) * mm});
            skLineSegment(sketch, "E113.bottom", {"start": v(1050, -2700) * mm, "end": v(900, -2700) * mm});
            skLineSegment(sketch, "E113.top", {"start": v(1050, -3100) * mm, "end": v(900, -3100) * mm});
            skLineSegment(sketch, "E113.left", {"start": v(1050, -2700) * mm, "end": v(1050, -3100) * mm});
            skLineSegment(sketch, "E113.right", {"start": v(900, -2700) * mm, "end": v(900, -3100) * mm});
            skSolve(sketch);
        }
        {
            var Q0;
            Q0 = qSketchRegion(id + "F105", true);
            extrude(context, id + "F106", {"entities" : qUnion([Q0]), "operationType" : NewBodyOperationType.REMOVE, "oppositeDirection" : true, "depth" : 250 * mm});
        }
        {
            var Q0;
            Q0=makeQuery(id+"F106.boolean.opBoolean","COPY",EDGE,{"derivedFrom":makeQuery(id+"F106.opExtrude","SWEPT_EDGE",EDGE,{"disambiguationData":[OSD([sQuery(id+"F105.wireOp",EDGE,"E113.bottom"),sQuery(id+"F105.wireOp",EDGE,"E113.right")])]})});
            var Q1;
            Q1=makeQuery(id+"F106.boolean.opBoolean","COPY",EDGE,{"derivedFrom":makeQuery(id+"F106.opExtrude","SWEPT_EDGE",EDGE,{"disambiguationData":[OSD([sQuery(id+"F105.wireOp",EDGE,"E113.bottom"),sQuery(id+"F105.wireOp",EDGE,"E113.left")])]})});
            var Q2;
            Q2=makeQuery(id+"F106.boolean.opBoolean","COPY",EDGE,{"derivedFrom":makeQuery(id+"F106.opExtrude","SWEPT_EDGE",EDGE,{"disambiguationData":[OSD([sQuery(id+"F105.wireOp",EDGE,"E113.top"),sQuery(id+"F105.wireOp",EDGE,"E113.left")])]})});
            var Q3;
            Q3=makeQuery(id+"F106.boolean.opBoolean","COPY",EDGE,{"derivedFrom":makeQuery(id+"F106.opExtrude","SWEPT_EDGE",EDGE,{"disambiguationData":[OSD([sQuery(id+"F105.wireOp",EDGE,"E113.top"),sQuery(id+"F105.wireOp",EDGE,"E113.right")])]})});
            var Q4;
            Q4=makeQuery(id+"F106.boolean.opBoolean","COPY",EDGE,{"derivedFrom":makeQuery(id+"F106.opExtrude","SWEPT_EDGE",EDGE,{"disambiguationData":[OSD([sQuery(id+"F105.wireOp",EDGE,"E112.bottom"),sQuery(id+"F105.wireOp",EDGE,"E112.right")])]})});
            var Q5;
            Q5=makeQuery(id+"F106.boolean.opBoolean","COPY",EDGE,{"derivedFrom":makeQuery(id+"F106.opExtrude","SWEPT_EDGE",EDGE,{"disambiguationData":[OSD([sQuery(id+"F105.wireOp",EDGE,"E112.top"),sQuery(id+"F105.wireOp",EDGE,"E112.right")])]})});
            var Q6;
            Q6=makeQuery(id+"F106.boolean.opBoolean","COPY",EDGE,{"derivedFrom":makeQuery(id+"F106.opExtrude","SWEPT_EDGE",EDGE,{"disambiguationData":[OSD([sQuery(id+"F105.wireOp",EDGE,"E112.bottom"),sQuery(id+"F105.wireOp",EDGE,"E112.left")])]})});
            var Q7;
            Q7=makeQuery(id+"F106.boolean.opBoolean","COPY",EDGE,{"derivedFrom":makeQuery(id+"F106.opExtrude","SWEPT_EDGE",EDGE,{"disambiguationData":[OSD([sQuery(id+"F105.wireOp",EDGE,"E112.top"),sQuery(id+"F105.wireOp",EDGE,"E112.left")])]})});
            fillet(context, id + "F107", {"entities" : qUnion([Q0, Q1, Q2, Q3, Q4, Q5, Q6, Q7]), "radius" : 50 * mm, "tangentPropagation" : true, "allowEdgeOverflow" : false});
        }
        {
            var Q0;
            Q0=makeQuery(id+"F106.boolean.opBoolean","COPY",FACE,{"derivedFrom":makeQuery(id+"F106.opExtrude","CAP_FACE",FACE,{"disambiguationData":[OSD([sQuery(id+"F105.wireOp",EDGE,"E113.bottom"),sQuery(id+"F105.wireOp",EDGE,"E113.top"),sQuery(id+"F105.wireOp",EDGE,"E113.left"),sQuery(id+"F105.wireOp",EDGE,"E113.right")])],"isStart":false})});
            var sketch = newSketch(context, id + "F108", { "sketchPlane" : qUnion([Q0])});
            skCircle(sketch, "E114", {"center": v(975, -3000) * mm, "radius": 40 * mm});
            skCircle(sketch, "E115", {"center": v(1175, -3000) * mm, "radius": 40 * mm});
            skSolve(sketch);
        }
        {
            var Q0;
            Q0 = qSketchRegion(id + "F108", true);
            extrude(context, id + "F109", {"entities" : qUnion([Q0]), "operationType" : NewBodyOperationType.REMOVE, "oppositeDirection" : true, "depth" : 10 * mm});
        }
        {
            var Q0;
            Q0=makeQuery(id+"F103.opExtrude","CAP_FACE",FACE,{"disambiguationData":[OSD([sQuery(id+"F102.wireOp",EDGE,"E111.bottom"),sQuery(id+"F102.wireOp",EDGE,"E111.top"),sQuery(id+"F102.wireOp",EDGE,"E111.left"),sQuery(id+"F102.wireOp",EDGE,"E111.right")])],"isStart":false});
            var sketch = newSketch(context, id + "F110", { "sketchPlane" : qUnion([Q0])});
            skCircle(sketch, "E116", {"center": v(1075, -3110) * mm, "radius": 20 * mm});
            skSolve(sketch);
        }
        {
            var Q0;
            Q0 = qSketchRegion(id + "F110", true);
            extrude(context, id + "F111", {"entities" : qUnion([Q0]), "operationType" : NewBodyOperationType.ADD, "depth" : 200 * mm});
        }
        {
            var Q0;
            Q0=makeQuery(id+"F111.opExtrude","CAP_FACE",FACE,{"disambiguationData":[OSD([sQuery(id+"F110.wireOp",EDGE,"E116")])],"isStart":false});
            var sketch = newSketch(context, id + "F112", { "sketchPlane" : qUnion([Q0])});
            skLineSegment(sketch, "E117.bottom", {"start": v(1095, -3130) * mm, "end": v(1055, -3130) * mm});
            skLineSegment(sketch, "E117.top", {"start": v(1095, -2880) * mm, "end": v(1055, -2880) * mm});
            skLineSegment(sketch, "E117.left", {"start": v(1095, -3130) * mm, "end": v(1095, -2880) * mm});
            skLineSegment(sketch, "E117.right", {"start": v(1055, -3130) * mm, "end": v(1055, -2880) * mm});
            skSolve(sketch);
        }
        {
            var Q0;
            Q0 = qSketchRegion(id + "F112", true);
            extrude(context, id + "F113", {"entities" : qUnion([Q0]), "operationType" : NewBodyOperationType.ADD, "depth" : 25 * mm});
        }
        {
            var Q0;
            Q0=qCreatedBy(makeId("Right.planeOp"),FACE);
            var sketch = newSketch(context, id + "F114", { "sketchPlane" : qUnion([Q0])});
            skLineSegment(sketch, "E118", {"start": v(-3800, 0) * mm, "end": v(-3800, 900) * mm});
            skLineSegment(sketch, "E119", {"start": v(-3800, 900) * mm, "end": v(-3775, 900) * mm});
            skLineSegment(sketch, "E120", {"start": v(-3775, 900) * mm, "end": v(-3775, 950) * mm});
            skLineSegment(sketch, "E121", {"start": v(-3775, 950) * mm, "end": v(-4425, 950) * mm});
            skLineSegment(sketch, "E122", {"start": v(-4425, 950) * mm, "end": v(-4425, 900) * mm});
            skLineSegment(sketch, "E123", {"start": v(-4425, 900) * mm, "end": v(-4400, 900) * mm});
            skLineSegment(sketch, "E124", {"start": v(-4400, 900) * mm, "end": v(-4400, 0) * mm});
            skLineSegment(sketch, "E125", {"start": v(-4400, 0) * mm, "end": v(-3800, 0) * mm});
            skSolve(sketch);
        }
        {
            var Q0;
            Q0 = qSketchRegion(id + "F114", true);
            extrude(context, id + "F115", {"entities" : qUnion([Q0]), "oppositeDirection" : true, "depth" : 1800 * mm});
        }
        {
            var Q0;
            Q0=makeQuery(id+"F92.opExtrude","SWEPT_FACE",FACE,{"disambiguationData":[OSD([sQuery(id+"F91.wireOp",EDGE,"E89")])]});
            var sketch = newSketch(context, id + "F116", { "sketchPlane" : qUnion([Q0])});
            skText(sketch, "E126", { "text": "60x65", "fontName": "OpenSans-Regular.ttf"});
            const initialGuessF116  = {"E126": [-0.58, -1.495, 1, 0, 0.1]};
            skSetInitialGuess(sketch, initialGuessF116);
            skSolve(sketch);
        }
        {
            var Q0;
            Q0 = qSketchRegion(id + "F116", true);
            extrude(context, id + "F117", {"entities" : qUnion([Q0]), "operationType" : NewBodyOperationType.REMOVE, "oppositeDirection" : true, "depth" : 10 * mm});
        }
        {
            var Q0;
            Q0=makeQuery(id+"F94.opExtrude","SWEPT_FACE",FACE,{"disambiguationData":[OSD([sQuery(id+"F93.wireOp",EDGE,"E97")])]});
            var sketch = newSketch(context, id + "F118", { "sketchPlane" : qUnion([Q0])});
            skText(sketch, "E127", { "text": "120x65", "fontName": "OpenSans-Regular.ttf"});
            const initialGuessF118  = {"E127": [-1.18, -2.695, 1, 0, 0.1]};
            skSetInitialGuess(sketch, initialGuessF118);
            skSolve(sketch);
        }
        {
            var Q0;
            Q0 = qSketchRegion(id + "F118", true);
            extrude(context, id + "F119", {"entities" : qUnion([Q0]), "operationType" : NewBodyOperationType.REMOVE, "oppositeDirection" : true, "depth" : 10 * mm});
        }
        {
            var Q0;
            Q0=makeQuery(id+"F115.opExtrude","SWEPT_FACE",FACE,{"disambiguationData":[OSD([sQuery(id+"F114.wireOp",EDGE,"E121")])]});
            var sketch = newSketch(context, id + "F120", { "sketchPlane" : qUnion([Q0])});
            skText(sketch, "E128", { "text": "180x65\n180x95", "fontName": "OpenSans-Regular.ttf"});
            const initialGuessF120  = {"E128": [-1.78, -3.895, 1, 0, 0.1]};
            skSetInitialGuess(sketch, initialGuessF120);
            skSolve(sketch);
        }
        {
            var Q0;
            Q0 = qSketchRegion(id + "F120", true);
            extrude(context, id + "F121", {"entities" : qUnion([Q0]), "operationType" : NewBodyOperationType.REMOVE, "oppositeDirection" : true, "depth" : 10 * mm});
        }
        {
            var Q0;
            {var subQ4=sQuery(id+"F114.wireOp",EDGE,"E121");var subQ5=sQuery(id+"F114.wireOp",EDGE,"E120");Q0=makeQuery(id+"F121.boolean.opBoolean","SPLIT",FACE,{"disambiguationData":[TD([makeQuery(id+"F115.opExtrude","SWEPT_FACE",FACE,{"disambiguationData":[OSD([subQ5])]})])],"derivedFrom":makeQuery(id+"F115.opExtrude","SWEPT_FACE",FACE,{"disambiguationData":[OSD([subQ4])]})});}
            var sketch = newSketch(context, id + "F122", { "sketchPlane" : qUnion([Q0])});
            skLineSegment(sketch, "E129", {"start": v(-1800, -4325) * mm, "end": v(0, -4325) * mm, "construction": true});
            skCircle(sketch, "E130", {"center": v(-1650, -4325) * mm, "radius": 25 * mm});
            skCircle(sketch, "E131", {"center": v(-900, -4325) * mm, "radius": 25 * mm});
            skCircle(sketch, "E132", {"center": v(-150, -4325) * mm, "radius": 25 * mm});
            skSolve(sketch);
        }
        {
            var Q0;
            Q0=makeQuery(id+"F115.opExtrude","CAP_FACE",FACE,{"disambiguationData":[OSD([sQuery(id+"F114.wireOp",EDGE,"E118"),sQuery(id+"F114.wireOp",EDGE,"E119"),sQuery(id+"F114.wireOp",EDGE,"E120"),sQuery(id+"F114.wireOp",EDGE,"E121"),sQuery(id+"F114.wireOp",EDGE,"E122"),sQuery(id+"F114.wireOp",EDGE,"E123"),sQuery(id+"F114.wireOp",EDGE,"E124"),sQuery(id+"F114.wireOp",EDGE,"E125")])],"isStart":true});
            var sketch = newSketch(context, id + "F123", { "sketchPlane" : qUnion([Q0])});
            skLineSegment(sketch, "E133", {"start": v(-4325, 950) * mm, "end": v(-4525, 1150) * mm});
            skLineSegment(sketch, "E134", {"start": v(-4325, 950) * mm, "end": v(-4536.6, 950) * mm, "construction": true});
            skSolve(sketch);
        }
        {
            var Q0;
            Q0 = qSketchRegion(id + "F122", true);
            var Q1;
            Q1 = qConstructionFilter(qBodyType(qCreatedBy(id + "F123" ,EDGE), BodyType.WIRE), ConstructionObject.NO);
            sweep(context, id + "F124", {"operationType" : NewBodyOperationType.ADD, "profiles" : qUnion([Q0]), "path" : qUnion([Q1])});
        }
        {
            var Q0;
            Q0=makeQuery(id+"F124.opSweep","CAP_FACE",FACE,{"disambiguationData":[OSD([sQuery(id+"F122.wireOp",EDGE,"E130"),sQuery(id+"F123.wireOp",VERTEX,"E133.end")])],"isStart":false});
            var sketch = newSketch(context, id + "F125", { "sketchPlane" : qUnion([Q0])});
            skLineSegment(sketch, "E135.bottom", {"start": v(-1800, -4725) * mm, "end": v(0, -4725) * mm});
            skLineSegment(sketch, "E135.top", {"start": v(-1800, -4325) * mm, "end": v(0, -4325) * mm});
            skLineSegment(sketch, "E135.left", {"start": v(-1800, -4725) * mm, "end": v(-1800, -4325) * mm});
            skLineSegment(sketch, "E135.right", {"start": v(0, -4725) * mm, "end": v(0, -4325) * mm});
            skSolve(sketch);
        }
        {
            var Q0;
            Q0 = qSketchRegion(id + "F125", true);
            extrude(context, id + "F126", {"entities" : qUnion([Q0]), "operationType" : NewBodyOperationType.ADD, "depth" : 20 * mm});
        }
        {
            var Q0;
            Q0=makeQuery(id+"F101.opPattern","COPY",BODY,{"derivedFrom":makeQuery(id+"F94.opExtrude","SWEPT_BODY",BODY,{"disambiguationData":[OSD([sQuery(id+"F93.wireOp",EDGE,"E94"),sQuery(id+"F93.wireOp",EDGE,"E95"),sQuery(id+"F93.wireOp",EDGE,"E96"),sQuery(id+"F93.wireOp",EDGE,"E97"),sQuery(id+"F93.wireOp",EDGE,"E98"),sQuery(id+"F93.wireOp",EDGE,"E99"),sQuery(id+"F93.wireOp",EDGE,"E100"),sQuery(id+"F93.wireOp",EDGE,"E101")])]}),"instanceName":"1"});
            transform(context, id + "F127", {"entities" : qUnion([Q0]), "transformType" : TransformType.TRANSLATION_3D, "dx" : 2000 * mm, "dy" : 0 * mm, "dz" : 0 * mm, "makeCopy" : true});
        }
        {
            var Q0;
            Q0=makeQuery(id+"F127.opPattern","COPY",FACE,{"derivedFrom":makeQuery(id+"F101.opPattern","COPY",FACE,{"derivedFrom":makeQuery(id+"F94.opExtrude","SWEPT_FACE",FACE,{"disambiguationData":[OSD([sQuery(id+"F93.wireOp",EDGE,"E98")])]}),"instanceName":"1"}),"instanceName":"1"});
            var sketch = newSketch(context, id + "F128", { "sketchPlane" : qUnion([Q0])});
            skLineSegment(sketch, "E136.bottom", {"start": v(2400, 900) * mm, "end": v(3600, 900) * mm});
            skLineSegment(sketch, "E136.top", {"start": v(2400, 1100) * mm, "end": v(3600, 1100) * mm});
            skLineSegment(sketch, "E136.left", {"start": v(2400, 900) * mm, "end": v(2400, 1100) * mm});
            skLineSegment(sketch, "E136.right", {"start": v(3600, 900) * mm, "end": v(3600, 1100) * mm});
            skSolve(sketch);
        }
        {
            var Q0;
            Q0 = qSketchRegion(id + "F128", true);
            extrude(context, id + "F129", {"entities" : qUnion([Q0]), "operationType" : NewBodyOperationType.ADD, "depth" : 10 * mm});
        }
        {
            var Q0;
            Q0=qCreatedBy(makeId("Top.planeOp"),FACE);
            var sketch = newSketch(context, id + "F130", { "sketchPlane" : qUnion([Q0])});
            skLineSegment(sketch, "E137.bottom", {"start": v(-2600, 2060) * mm, "end": v(-3050, 2060) * mm});
            skLineSegment(sketch, "E137.top", {"start": v(-2600, 1600) * mm, "end": v(-3050, 1600) * mm});
            skLineSegment(sketch, "E137.left", {"start": v(-2600, 2060) * mm, "end": v(-2600, 1600) * mm});
            skLineSegment(sketch, "E137.right", {"start": v(-3050, 2060) * mm, "end": v(-3050, 1600) * mm});
            skArc(sketch, "E138", {"start": v(-2600, 2060) * mm, "mid": v(-2825, 2110) * mm, "end": v(-3050, 2060) * mm});
            skArc(sketch, "E139", {"start": v(-3050, 1600) * mm, "mid": v(-2825, 1550) * mm, "end": v(-2600, 1600) * mm});
            skSolve(sketch);
        }
        {
            var Q0;
            Q0 = qSketchRegion(id + "F130", true);
            extrude(context, id + "F131", {"entities" : qUnion([Q0]), "depth" : 1170 * mm});
        }
        {
            var Q0;
            Q0=makeQuery(id+"F131.opExtrude","CAP_EDGE",EDGE,{"disambiguationData":[OSD([sQuery(id+"F130.wireOp",EDGE,"E137.left")])],"isStart":false});
            cPoint(context, id + "F132", {"entities" : qUnion([Q0]), "parameter" : 0.5});
        }
        {
            var Q0;
            Q0=makeQuery(id+"F131.opExtrude","CAP_EDGE",EDGE,{"disambiguationData":[OSD([sQuery(id+"F130.wireOp",EDGE,"E137.right")])],"isStart":false});
            cPoint(context, id + "F133", {"entities" : qUnion([Q0]), "parameter" : 0.5});
        }
        {
            var Q0;
            Q0=makeQuery(id+"F131.opExtrude","CAP_EDGE",EDGE,{"disambiguationData":[OSD([sQuery(id+"F130.wireOp",EDGE,"E137.left")])],"isStart":true});
            cPoint(context, id + "F134", {"entities" : qUnion([Q0]), "parameter" : 0.5});
        }
        {
            var Q0;
            Q0 = qCreatedBy(id + "F132" ,VERTEX);
            var Q1;
            Q1 = qCreatedBy(id + "F133" ,VERTEX);
            var Q2;
            Q2 = qCreatedBy(id + "F134" ,VERTEX);
            cPlane(context, id + "F135", {"entities" : qUnion([Q0, Q1, Q2]), "cplaneType" : CPlaneType.THREE_POINT, "offset" : 25 * mm, "width" : 150 * mm, "height" : 150 * mm});
        }
        {
            var Q0;
            Q0=qCreatedBy(id+"F135.planeOp",FACE);
            var sketch = newSketch(context, id + "F136", { "sketchPlane" : qUnion([Q0])});
            skLineSegment(sketch, "E140", {"start": v(2600, 1170) * mm, "end": v(2530, 1240) * mm});
            skLineSegment(sketch, "E141", {"start": v(2530, 1240) * mm, "end": v(2526.46, 1236.46) * mm});
            skLineSegment(sketch, "E142", {"start": v(2526.46, 1236.46) * mm, "end": v(2600, 1162.93) * mm});
            skLineSegment(sketch, "E143", {"start": v(2600, 1170) * mm, "end": v(2600, 1162.93) * mm});
            skSolve(sketch);
        }
        {
            var Q0;
            Q0 = qSketchRegion(id + "F136", true);
            extrude(context, id + "F137", {"entities" : qUnion([Q0]), "operationType" : NewBodyOperationType.ADD, "depth" : 190 * mm, "symmetric" : true});
        }
        {
            var Q0;
            Q0=makeQuery(id+"F137.opExtrude","CAP_EDGE",EDGE,{"disambiguationData":[OSD([sQuery(id+"F136.wireOp",EDGE,"E141")])],"isStart":false});
            var Q1;
            Q1=makeQuery(id+"F137.opExtrude","CAP_EDGE",EDGE,{"disambiguationData":[OSD([sQuery(id+"F136.wireOp",EDGE,"E141")])],"isStart":true});
            chamfer(context, id + "F138", {"entities" : qUnion([Q0, Q1]), "chamferType" : ChamferType.TWO_OFFSETS, "width1" : 100 * mm, "oppositeDirection" : false, "width2" : 20 * mm, "tangentPropagation" : true});
        }
        {
            var Q0;
            {var subQ0=sQuery(id+"F136.wireOp",EDGE,"E141");Q0=makeQuery(id+"F138.opChamfer","BLEND_EDGE",EDGE,{"blendedFrom":[makeQuery(id+"F137.opExtrude","CAP_EDGE",EDGE,{"disambiguationData":[OSD([subQ0])],"isStart":false}),makeQuery(id+"F137.opExtrude","SWEPT_FACE",FACE,{"disambiguationData":[OSD([subQ0])]})],"blendedInto":[makeQuery(id+"F137.opExtrude","SWEPT_FACE",FACE,{"disambiguationData":[OSD([subQ0])]})]});}
            var Q1;
            {var subQ0=sQuery(id+"F136.wireOp",EDGE,"E141");Q1=makeQuery(id+"F138.opChamfer","BLEND_EDGE",EDGE,{"blendedFrom":[makeQuery(id+"F137.opExtrude","CAP_EDGE",EDGE,{"disambiguationData":[OSD([subQ0])],"isStart":true}),makeQuery(id+"F137.opExtrude","SWEPT_FACE",FACE,{"disambiguationData":[OSD([subQ0])]})],"blendedInto":[makeQuery(id+"F137.opExtrude","SWEPT_FACE",FACE,{"disambiguationData":[OSD([subQ0])]})]});}
            fillet(context, id + "F139", {"entities" : qUnion([Q0, Q1]), "radius" : 5 * mm, "tangentPropagation" : true, "allowEdgeOverflow" : false});
        }
        {
            var Q0;
            Q0=makeQuery(id+"F131.opExtrude","SWEPT_FACE",FACE,{"disambiguationData":[OSD([sQuery(id+"F130.wireOp",EDGE,"E137.right")])]});
            var sketch = newSketch(context, id + "F140", { "sketchPlane" : qUnion([Q0])});
            skLineSegment(sketch, "E144.bottom", {"start": v(-1730, 870) * mm, "end": v(-1930, 870) * mm});
            skLineSegment(sketch, "E144.top", {"start": v(-1730, 470) * mm, "end": v(-1930, 470) * mm});
            skLineSegment(sketch, "E144.left", {"start": v(-1730, 870) * mm, "end": v(-1730, 470) * mm});
            skLineSegment(sketch, "E144.right", {"start": v(-1930, 870) * mm, "end": v(-1930, 470) * mm});
            skLineSegment(sketch, "E145", {"start": v(-1830, 1170) * mm, "end": v(-1830, 0) * mm, "construction": true});
            skSolve(sketch);
        }
        {
            var Q0;
            Q0 = qSketchRegion(id + "F140", true);
            extrude(context, id + "F141", {"entities" : qUnion([Q0]), "operationType" : NewBodyOperationType.REMOVE, "oppositeDirection" : true, "depth" : 25 * mm});
        }
        {
            var Q0;
            Q0=qCreatedBy(makeId("Top.planeOp"),FACE);
            var sketch = newSketch(context, id + "F142", { "sketchPlane" : qUnion([Q0])});
            skLineSegment(sketch, "E146.bottom", {"start": v(-2050, 3050) * mm, "end": v(-2000, 3050) * mm});
            skLineSegment(sketch, "E146.top", {"start": v(-2050, 3000) * mm, "end": v(-2000, 3000) * mm});
            skLineSegment(sketch, "E146.left", {"start": v(-2050, 3050) * mm, "end": v(-2050, 3000) * mm});
            skLineSegment(sketch, "E146.right", {"start": v(-2000, 3050) * mm, "end": v(-2000, 3000) * mm});
            skLineSegment(sketch, "E147.0.1.0", {"start": v(-2000, 4200) * mm, "end": v(-2000, 4150) * mm});
            skLineSegment(sketch, "E147.0.1.1", {"start": v(-2050, 4200) * mm, "end": v(-2000, 4200) * mm});
            skLineSegment(sketch, "E147.0.1.2", {"start": v(-2050, 4200) * mm, "end": v(-2050, 4150) * mm});
            skLineSegment(sketch, "E147.0.1.3", {"start": v(-2050, 4150) * mm, "end": v(-2000, 4150) * mm});
            skLineSegment(sketch, "E147.1.0.0", {"start": v(-2700, 3050) * mm, "end": v(-2700, 3000) * mm});
            skLineSegment(sketch, "E147.1.0.1", {"start": v(-2750, 3050) * mm, "end": v(-2700, 3050) * mm});
            skLineSegment(sketch, "E147.1.0.2", {"start": v(-2750, 3050) * mm, "end": v(-2750, 3000) * mm});
            skLineSegment(sketch, "E147.1.0.3", {"start": v(-2750, 3000) * mm, "end": v(-2700, 3000) * mm});
            skLineSegment(sketch, "E147.1.1.0", {"start": v(-2700, 4200) * mm, "end": v(-2700, 4150) * mm});
            skLineSegment(sketch, "E147.1.1.1", {"start": v(-2750, 4200) * mm, "end": v(-2700, 4200) * mm});
            skLineSegment(sketch, "E147.1.1.2", {"start": v(-2750, 4200) * mm, "end": v(-2750, 4150) * mm});
            skLineSegment(sketch, "E147.1.1.3", {"start": v(-2750, 4150) * mm, "end": v(-2700, 4150) * mm});
            skLineSegment(sketch, "E147.direction1", {"start": v(-2050, 3000) * mm, "end": v(-2750, 3000) * mm, "construction": true});
            skLineSegment(sketch, "E147.direction2", {"start": v(-2050, 3000) * mm, "end": v(-2050, 4150) * mm, "construction": true});
            skSolve(sketch);
        }
        {
            var Q0;
            Q0 = qSketchRegion(id + "F142", true);
            extrude(context, id + "F143", {"entities" : qUnion([Q0]), "depth" : 500 * mm});
        }
        {
            var Q0;
            Q0=makeQuery(id+"F143.opExtrude","CAP_FACE",FACE,{"disambiguationData":[OSD([sQuery(id+"F142.wireOp",EDGE,"E147.1.1.0"),sQuery(id+"F142.wireOp",EDGE,"E147.1.1.1"),sQuery(id+"F142.wireOp",EDGE,"E147.1.1.2"),sQuery(id+"F142.wireOp",EDGE,"E147.1.1.3")])],"isStart":false});
            var sketch = newSketch(context, id + "F144", { "sketchPlane" : qUnion([Q0])});
            skLineSegment(sketch, "E148.bottom", {"start": v(-2750, 4200) * mm, "end": v(-2000, 4200) * mm});
            skLineSegment(sketch, "E148.top", {"start": v(-2750, 3000) * mm, "end": v(-2000, 3000) * mm});
            skLineSegment(sketch, "E148.left", {"start": v(-2750, 4200) * mm, "end": v(-2750, 3000) * mm});
            skLineSegment(sketch, "E148.right", {"start": v(-2000, 4200) * mm, "end": v(-2000, 3000) * mm});
            skSolve(sketch);
        }
        {
            var Q0;
            Q0 = qSketchRegion(id + "F144", true);
            extrude(context, id + "F145", {"entities" : qUnion([Q0]), "operationType" : NewBodyOperationType.ADD, "depth" : 50 * mm});
        }
        {
            var Q0;
            Q0=qCreatedBy(makeId("Top.planeOp"),FACE);
            var sketch = newSketch(context, id + "F146", { "sketchPlane" : qUnion([Q0])});
            skLineSegment(sketch, "E149.bottom", {"start": v(2400, -2000) * mm, "end": v(3400, -2000) * mm});
            skLineSegment(sketch, "E149.top", {"start": v(2400, -1400) * mm, "end": v(3400, -1400) * mm});
            skLineSegment(sketch, "E149.left", {"start": v(2400, -2000) * mm, "end": v(2400, -1400) * mm});
            skLineSegment(sketch, "E149.right", {"start": v(3400, -2000) * mm, "end": v(3400, -1400) * mm});
            skSolve(sketch);
        }
        {
            var Q0;
            Q0 = qSketchRegion(id + "F146", true);
            extrude(context, id + "F147", {"entities" : qUnion([Q0]), "depth" : 900 * mm});
        }
        {
            var Q0;
            Q0=makeQuery(id+"F147.opExtrude","CAP_FACE",FACE,{"disambiguationData":[OSD([sQuery(id+"F146.wireOp",EDGE,"E149.bottom"),sQuery(id+"F146.wireOp",EDGE,"E149.top"),sQuery(id+"F146.wireOp",EDGE,"E149.left"),sQuery(id+"F146.wireOp",EDGE,"E149.right")])],"isStart":false});
            var sketch = newSketch(context, id + "F148", { "sketchPlane" : qUnion([Q0])});
            skLineSegment(sketch, "E150.bottom", {"start": v(2000, -2025) * mm, "end": v(3800, -2025) * mm});
            skLineSegment(sketch, "E150.top", {"start": v(2000, -1000) * mm, "end": v(3800, -1000) * mm});
            skLineSegment(sketch, "E150.left", {"start": v(2000, -2025) * mm, "end": v(2000, -1000) * mm});
            skLineSegment(sketch, "E150.right", {"start": v(3800, -2025) * mm, "end": v(3800, -1000) * mm});
            skSolve(sketch);
        }
        {
            var Q0;
            Q0 = qSketchRegion(id + "F148", true);
            extrude(context, id + "F149", {"entities" : qUnion([Q0]), "operationType" : NewBodyOperationType.ADD, "depth" : 25 * mm});
        }
        {
            var Q0;
            Q0=makeQuery(id+"F149.opExtrude","CAP_FACE",FACE,{"disambiguationData":[OSD([sQuery(id+"F148.wireOp",EDGE,"E150.bottom"),sQuery(id+"F148.wireOp",EDGE,"E150.top"),sQuery(id+"F148.wireOp",EDGE,"E150.left"),sQuery(id+"F148.wireOp",EDGE,"E150.right")])],"isStart":false});
            var sketch = newSketch(context, id + "F150", { "sketchPlane" : qUnion([Q0])});
            skLineSegment(sketch, "E151.bottom", {"start": v(2500, -1975) * mm, "end": v(3300, -1975) * mm});
            skLineSegment(sketch, "E151.top", {"start": v(2500, -1575) * mm, "end": v(3300, -1575) * mm});
            skLineSegment(sketch, "E151.left", {"start": v(2500, -1975) * mm, "end": v(2500, -1575) * mm});
            skLineSegment(sketch, "E151.right", {"start": v(3300, -1975) * mm, "end": v(3300, -1575) * mm});
            skSolve(sketch);
        }
        {
            var Q0;
            Q0 = qSketchRegion(id + "F150", true);
            extrude(context, id + "F151", {"entities" : qUnion([Q0]), "operationType" : NewBodyOperationType.ADD, "depth" : 10 * mm});
        }
        {
            var Q0;
            Q0=makeQuery(id+"F151.opExtrude","CAP_FACE",FACE,{"disambiguationData":[OSD([sQuery(id+"F150.wireOp",EDGE,"E151.bottom"),sQuery(id+"F150.wireOp",EDGE,"E151.top"),sQuery(id+"F150.wireOp",EDGE,"E151.left"),sQuery(id+"F150.wireOp",EDGE,"E151.right")])],"isStart":false});
            var sketch = newSketch(context, id + "F152", { "sketchPlane" : qUnion([Q0])});
            skCircle(sketch, "E152", {"center": v(2900, -1735) * mm, "radius": 90 * mm});
            skCircle(sketch, "E153", {"center": v(3190, -1675) * mm, "radius": 30 * mm});
            skCircle(sketch, "E154", {"center": v(3190, -1815) * mm, "radius": 60 * mm});
            skCircle(sketch, "E155", {"center": v(2610, -1675) * mm, "radius": 30 * mm});
            skCircle(sketch, "E156", {"center": v(2610, -1815) * mm, "radius": 60 * mm});
            skSolve(sketch);
        }
        {
            var Q0;
            Q0 = qSketchRegion(id + "F152", true);
            extrude(context, id + "F153", {"entities" : qUnion([Q0]), "operationType" : NewBodyOperationType.REMOVE, "oppositeDirection" : true, "depth" : 10 * mm});
        }
    });
